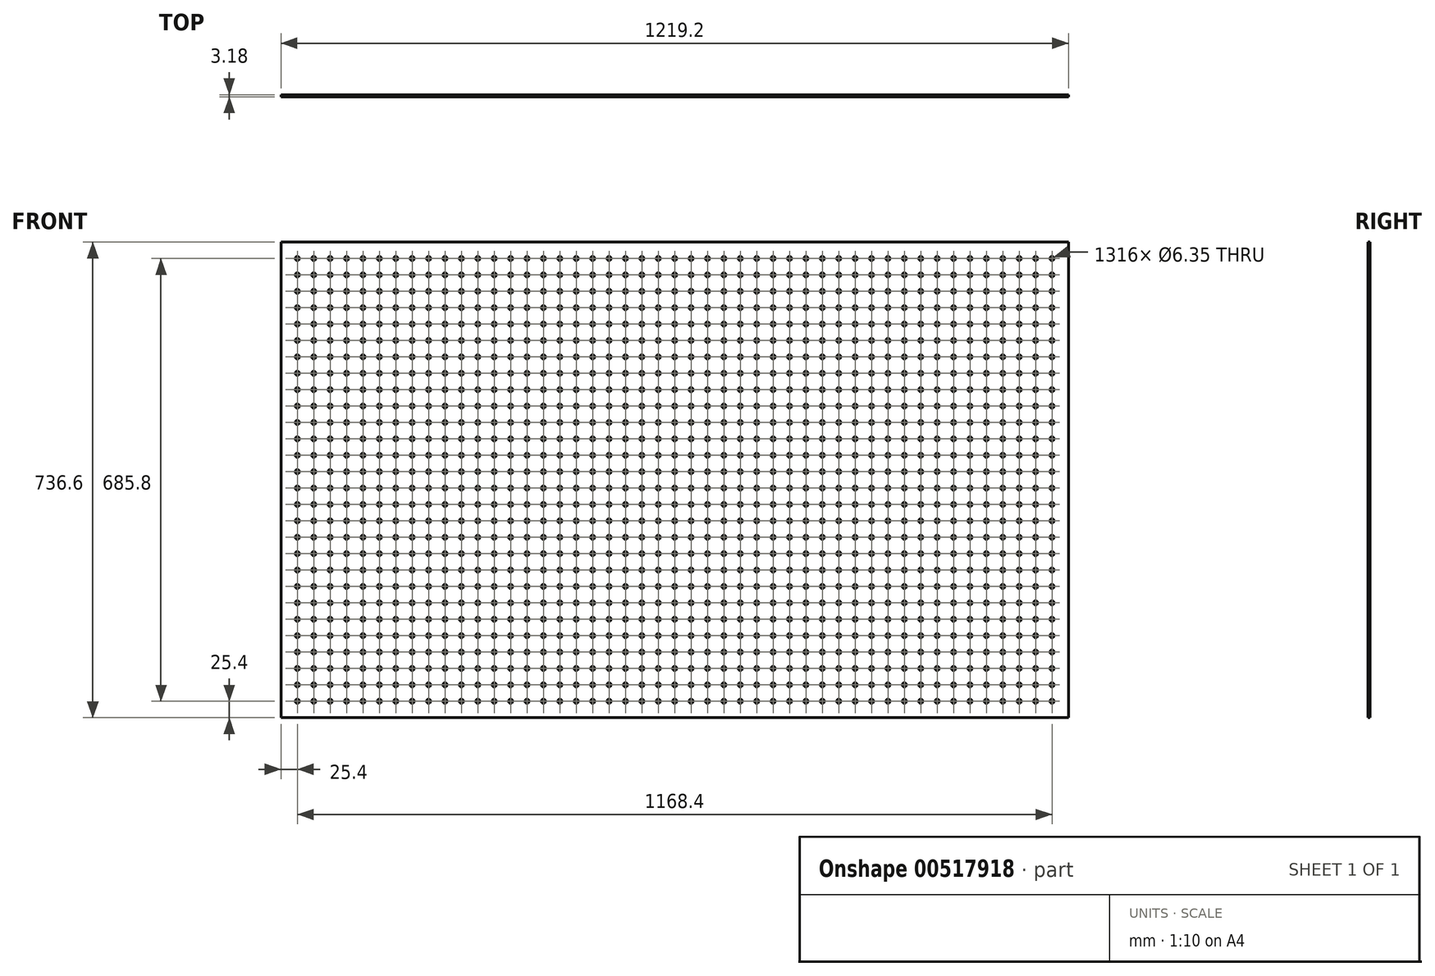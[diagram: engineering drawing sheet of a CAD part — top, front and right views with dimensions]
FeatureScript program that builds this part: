
annotation { "Feature Type Name" : "Feature", "Feature Type Description" : "" }
export const myFeature = defineFeature(function(context is Context, id is Id, definition is map)
    precondition{}
    {
        {
            var Q0;
            Q0=qCreatedBy(makeId("Front.planeOp"),FACE);
            var sketch = newSketch(context, id + "F0", { "sketchPlane" : qUnion([Q0])});
            skLineSegment(sketch, "E0.bottom", {"start": v(609.6, 368.3) * mm, "end": v(-609.6, 368.3) * mm});
            skLineSegment(sketch, "E0.top", {"start": v(609.6, -368.3) * mm, "end": v(-609.6, -368.3) * mm});
            skLineSegment(sketch, "E0.left", {"start": v(609.6, 368.3) * mm, "end": v(609.6, -368.3) * mm});
            skLineSegment(sketch, "E0.right", {"start": v(-609.6, 368.3) * mm, "end": v(-609.6, -368.3) * mm});
            skPoint(sketch, "E0.middle", {"position": v(0, 0) * mm});
            skCircle(sketch, "E1", {"center": v(-584.2, 342.9) * mm, "radius": 3.18 * mm});
            skCircle(sketch, "E2.0.1.0", {"center": v(-584.2, 317.5) * mm, "radius": 3.18 * mm});
            skCircle(sketch, "E2.0.2.0", {"center": v(-584.2, 292.1) * mm, "radius": 3.18 * mm});
            skCircle(sketch, "E2.0.3.0", {"center": v(-584.2, 266.7) * mm, "radius": 3.18 * mm});
            skCircle(sketch, "E2.0.4.0", {"center": v(-584.2, 241.3) * mm, "radius": 3.18 * mm});
            skCircle(sketch, "E2.0.5.0", {"center": v(-584.2, 215.9) * mm, "radius": 3.18 * mm});
            skCircle(sketch, "E2.0.6.0", {"center": v(-584.2, 190.5) * mm, "radius": 3.18 * mm});
            skCircle(sketch, "E2.0.7.0", {"center": v(-584.2, 165.1) * mm, "radius": 3.18 * mm});
            skCircle(sketch, "E2.0.8.0", {"center": v(-584.2, 139.7) * mm, "radius": 3.18 * mm});
            skCircle(sketch, "E2.0.9.0", {"center": v(-584.2, 114.3) * mm, "radius": 3.18 * mm});
            skCircle(sketch, "E2.0.10.0", {"center": v(-584.2, 88.9) * mm, "radius": 3.18 * mm});
            skCircle(sketch, "E2.0.11.0", {"center": v(-584.2, 63.5) * mm, "radius": 3.18 * mm});
            skCircle(sketch, "E2.0.12.0", {"center": v(-584.2, 38.1) * mm, "radius": 3.18 * mm});
            skCircle(sketch, "E2.0.13.0", {"center": v(-584.2, 12.7) * mm, "radius": 3.18 * mm});
            skCircle(sketch, "E2.0.14.0", {"center": v(-584.2, -12.7) * mm, "radius": 3.18 * mm});
            skCircle(sketch, "E2.0.15.0", {"center": v(-584.2, -38.1) * mm, "radius": 3.18 * mm});
            skCircle(sketch, "E2.0.16.0", {"center": v(-584.2, -63.5) * mm, "radius": 3.18 * mm});
            skCircle(sketch, "E2.0.17.0", {"center": v(-584.2, -88.9) * mm, "radius": 3.18 * mm});
            skCircle(sketch, "E2.0.18.0", {"center": v(-584.2, -114.3) * mm, "radius": 3.18 * mm});
            skCircle(sketch, "E2.0.19.0", {"center": v(-584.2, -139.7) * mm, "radius": 3.18 * mm});
            skCircle(sketch, "E2.0.20.0", {"center": v(-584.2, -165.1) * mm, "radius": 3.18 * mm});
            skCircle(sketch, "E2.0.21.0", {"center": v(-584.2, -190.5) * mm, "radius": 3.18 * mm});
            skCircle(sketch, "E2.0.22.0", {"center": v(-584.2, -215.9) * mm, "radius": 3.18 * mm});
            skCircle(sketch, "E2.0.23.0", {"center": v(-584.2, -241.3) * mm, "radius": 3.18 * mm});
            skCircle(sketch, "E2.0.24.0", {"center": v(-584.2, -266.7) * mm, "radius": 3.18 * mm});
            skCircle(sketch, "E2.0.25.0", {"center": v(-584.2, -292.1) * mm, "radius": 3.18 * mm});
            skCircle(sketch, "E2.0.26.0", {"center": v(-584.2, -317.5) * mm, "radius": 3.18 * mm});
            skCircle(sketch, "E2.0.27.0", {"center": v(-584.2, -342.9) * mm, "radius": 3.18 * mm});
            skCircle(sketch, "E2.1.0.0", {"center": v(-558.8, 342.9) * mm, "radius": 3.18 * mm});
            skCircle(sketch, "E2.1.1.0", {"center": v(-558.8, 317.5) * mm, "radius": 3.18 * mm});
            skCircle(sketch, "E2.1.2.0", {"center": v(-558.8, 292.1) * mm, "radius": 3.18 * mm});
            skCircle(sketch, "E2.1.3.0", {"center": v(-558.8, 266.7) * mm, "radius": 3.18 * mm});
            skCircle(sketch, "E2.1.4.0", {"center": v(-558.8, 241.3) * mm, "radius": 3.18 * mm});
            skCircle(sketch, "E2.1.5.0", {"center": v(-558.8, 215.9) * mm, "radius": 3.18 * mm});
            skCircle(sketch, "E2.1.6.0", {"center": v(-558.8, 190.5) * mm, "radius": 3.18 * mm});
            skCircle(sketch, "E2.1.7.0", {"center": v(-558.8, 165.1) * mm, "radius": 3.18 * mm});
            skCircle(sketch, "E2.1.8.0", {"center": v(-558.8, 139.7) * mm, "radius": 3.18 * mm});
            skCircle(sketch, "E2.1.9.0", {"center": v(-558.8, 114.3) * mm, "radius": 3.18 * mm});
            skCircle(sketch, "E2.1.10.0", {"center": v(-558.8, 88.9) * mm, "radius": 3.18 * mm});
            skCircle(sketch, "E2.1.11.0", {"center": v(-558.8, 63.5) * mm, "radius": 3.18 * mm});
            skCircle(sketch, "E2.1.12.0", {"center": v(-558.8, 38.1) * mm, "radius": 3.18 * mm});
            skCircle(sketch, "E2.1.13.0", {"center": v(-558.8, 12.7) * mm, "radius": 3.18 * mm});
            skCircle(sketch, "E2.1.14.0", {"center": v(-558.8, -12.7) * mm, "radius": 3.18 * mm});
            skCircle(sketch, "E2.1.15.0", {"center": v(-558.8, -38.1) * mm, "radius": 3.18 * mm});
            skCircle(sketch, "E2.1.16.0", {"center": v(-558.8, -63.5) * mm, "radius": 3.18 * mm});
            skCircle(sketch, "E2.1.17.0", {"center": v(-558.8, -88.9) * mm, "radius": 3.18 * mm});
            skCircle(sketch, "E2.1.18.0", {"center": v(-558.8, -114.3) * mm, "radius": 3.18 * mm});
            skCircle(sketch, "E2.1.19.0", {"center": v(-558.8, -139.7) * mm, "radius": 3.18 * mm});
            skCircle(sketch, "E2.1.20.0", {"center": v(-558.8, -165.1) * mm, "radius": 3.18 * mm});
            skCircle(sketch, "E2.1.21.0", {"center": v(-558.8, -190.5) * mm, "radius": 3.18 * mm});
            skCircle(sketch, "E2.1.22.0", {"center": v(-558.8, -215.9) * mm, "radius": 3.18 * mm});
            skCircle(sketch, "E2.1.23.0", {"center": v(-558.8, -241.3) * mm, "radius": 3.18 * mm});
            skCircle(sketch, "E2.1.24.0", {"center": v(-558.8, -266.7) * mm, "radius": 3.18 * mm});
            skCircle(sketch, "E2.1.25.0", {"center": v(-558.8, -292.1) * mm, "radius": 3.18 * mm});
            skCircle(sketch, "E2.1.26.0", {"center": v(-558.8, -317.5) * mm, "radius": 3.18 * mm});
            skCircle(sketch, "E2.1.27.0", {"center": v(-558.8, -342.9) * mm, "radius": 3.18 * mm});
            skCircle(sketch, "E2.2.0.0", {"center": v(-533.4, 342.9) * mm, "radius": 3.18 * mm});
            skCircle(sketch, "E2.2.1.0", {"center": v(-533.4, 317.5) * mm, "radius": 3.18 * mm});
            skCircle(sketch, "E2.2.2.0", {"center": v(-533.4, 292.1) * mm, "radius": 3.18 * mm});
            skCircle(sketch, "E2.2.3.0", {"center": v(-533.4, 266.7) * mm, "radius": 3.18 * mm});
            skCircle(sketch, "E2.2.4.0", {"center": v(-533.4, 241.3) * mm, "radius": 3.18 * mm});
            skCircle(sketch, "E2.2.5.0", {"center": v(-533.4, 215.9) * mm, "radius": 3.18 * mm});
            skCircle(sketch, "E2.2.6.0", {"center": v(-533.4, 190.5) * mm, "radius": 3.18 * mm});
            skCircle(sketch, "E2.2.7.0", {"center": v(-533.4, 165.1) * mm, "radius": 3.18 * mm});
            skCircle(sketch, "E2.2.8.0", {"center": v(-533.4, 139.7) * mm, "radius": 3.18 * mm});
            skCircle(sketch, "E2.2.9.0", {"center": v(-533.4, 114.3) * mm, "radius": 3.18 * mm});
            skCircle(sketch, "E2.2.10.0", {"center": v(-533.4, 88.9) * mm, "radius": 3.18 * mm});
            skCircle(sketch, "E2.2.11.0", {"center": v(-533.4, 63.5) * mm, "radius": 3.18 * mm});
            skCircle(sketch, "E2.2.12.0", {"center": v(-533.4, 38.1) * mm, "radius": 3.18 * mm});
            skCircle(sketch, "E2.2.13.0", {"center": v(-533.4, 12.7) * mm, "radius": 3.18 * mm});
            skCircle(sketch, "E2.2.14.0", {"center": v(-533.4, -12.7) * mm, "radius": 3.18 * mm});
            skCircle(sketch, "E2.2.15.0", {"center": v(-533.4, -38.1) * mm, "radius": 3.18 * mm});
            skCircle(sketch, "E2.2.16.0", {"center": v(-533.4, -63.5) * mm, "radius": 3.18 * mm});
            skCircle(sketch, "E2.2.17.0", {"center": v(-533.4, -88.9) * mm, "radius": 3.18 * mm});
            skCircle(sketch, "E2.2.18.0", {"center": v(-533.4, -114.3) * mm, "radius": 3.18 * mm});
            skCircle(sketch, "E2.2.19.0", {"center": v(-533.4, -139.7) * mm, "radius": 3.18 * mm});
            skCircle(sketch, "E2.2.20.0", {"center": v(-533.4, -165.1) * mm, "radius": 3.18 * mm});
            skCircle(sketch, "E2.2.21.0", {"center": v(-533.4, -190.5) * mm, "radius": 3.18 * mm});
            skCircle(sketch, "E2.2.22.0", {"center": v(-533.4, -215.9) * mm, "radius": 3.18 * mm});
            skCircle(sketch, "E2.2.23.0", {"center": v(-533.4, -241.3) * mm, "radius": 3.18 * mm});
            skCircle(sketch, "E2.2.24.0", {"center": v(-533.4, -266.7) * mm, "radius": 3.18 * mm});
            skCircle(sketch, "E2.2.25.0", {"center": v(-533.4, -292.1) * mm, "radius": 3.18 * mm});
            skCircle(sketch, "E2.2.26.0", {"center": v(-533.4, -317.5) * mm, "radius": 3.18 * mm});
            skCircle(sketch, "E2.2.27.0", {"center": v(-533.4, -342.9) * mm, "radius": 3.18 * mm});
            skCircle(sketch, "E2.3.0.0", {"center": v(-508, 342.9) * mm, "radius": 3.18 * mm});
            skCircle(sketch, "E2.3.1.0", {"center": v(-508, 317.5) * mm, "radius": 3.18 * mm});
            skCircle(sketch, "E2.3.2.0", {"center": v(-508, 292.1) * mm, "radius": 3.18 * mm});
            skCircle(sketch, "E2.3.3.0", {"center": v(-508, 266.7) * mm, "radius": 3.18 * mm});
            skCircle(sketch, "E2.3.4.0", {"center": v(-508, 241.3) * mm, "radius": 3.18 * mm});
            skCircle(sketch, "E2.3.5.0", {"center": v(-508, 215.9) * mm, "radius": 3.18 * mm});
            skCircle(sketch, "E2.3.6.0", {"center": v(-508, 190.5) * mm, "radius": 3.18 * mm});
            skCircle(sketch, "E2.3.7.0", {"center": v(-508, 165.1) * mm, "radius": 3.18 * mm});
            skCircle(sketch, "E2.3.8.0", {"center": v(-508, 139.7) * mm, "radius": 3.18 * mm});
            skCircle(sketch, "E2.3.9.0", {"center": v(-508, 114.3) * mm, "radius": 3.18 * mm});
            skCircle(sketch, "E2.3.10.0", {"center": v(-508, 88.9) * mm, "radius": 3.18 * mm});
            skCircle(sketch, "E2.3.11.0", {"center": v(-508, 63.5) * mm, "radius": 3.18 * mm});
            skCircle(sketch, "E2.3.12.0", {"center": v(-508, 38.1) * mm, "radius": 3.18 * mm});
            skCircle(sketch, "E2.3.13.0", {"center": v(-508, 12.7) * mm, "radius": 3.18 * mm});
            skCircle(sketch, "E2.3.14.0", {"center": v(-508, -12.7) * mm, "radius": 3.18 * mm});
            skCircle(sketch, "E2.3.15.0", {"center": v(-508, -38.1) * mm, "radius": 3.18 * mm});
            skCircle(sketch, "E2.3.16.0", {"center": v(-508, -63.5) * mm, "radius": 3.18 * mm});
            skCircle(sketch, "E2.3.17.0", {"center": v(-508, -88.9) * mm, "radius": 3.18 * mm});
            skCircle(sketch, "E2.3.18.0", {"center": v(-508, -114.3) * mm, "radius": 3.18 * mm});
            skCircle(sketch, "E2.3.19.0", {"center": v(-508, -139.7) * mm, "radius": 3.18 * mm});
            skCircle(sketch, "E2.3.20.0", {"center": v(-508, -165.1) * mm, "radius": 3.18 * mm});
            skCircle(sketch, "E2.3.21.0", {"center": v(-508, -190.5) * mm, "radius": 3.18 * mm});
            skCircle(sketch, "E2.3.22.0", {"center": v(-508, -215.9) * mm, "radius": 3.18 * mm});
            skCircle(sketch, "E2.3.23.0", {"center": v(-508, -241.3) * mm, "radius": 3.18 * mm});
            skCircle(sketch, "E2.3.24.0", {"center": v(-508, -266.7) * mm, "radius": 3.18 * mm});
            skCircle(sketch, "E2.3.25.0", {"center": v(-508, -292.1) * mm, "radius": 3.18 * mm});
            skCircle(sketch, "E2.3.26.0", {"center": v(-508, -317.5) * mm, "radius": 3.18 * mm});
            skCircle(sketch, "E2.3.27.0", {"center": v(-508, -342.9) * mm, "radius": 3.18 * mm});
            skCircle(sketch, "E2.4.0.0", {"center": v(-482.6, 342.9) * mm, "radius": 3.18 * mm});
            skCircle(sketch, "E2.4.1.0", {"center": v(-482.6, 317.5) * mm, "radius": 3.18 * mm});
            skCircle(sketch, "E2.4.2.0", {"center": v(-482.6, 292.1) * mm, "radius": 3.18 * mm});
            skCircle(sketch, "E2.4.3.0", {"center": v(-482.6, 266.7) * mm, "radius": 3.18 * mm});
            skCircle(sketch, "E2.4.4.0", {"center": v(-482.6, 241.3) * mm, "radius": 3.18 * mm});
            skCircle(sketch, "E2.4.5.0", {"center": v(-482.6, 215.9) * mm, "radius": 3.18 * mm});
            skCircle(sketch, "E2.4.6.0", {"center": v(-482.6, 190.5) * mm, "radius": 3.18 * mm});
            skCircle(sketch, "E2.4.7.0", {"center": v(-482.6, 165.1) * mm, "radius": 3.18 * mm});
            skCircle(sketch, "E2.4.8.0", {"center": v(-482.6, 139.7) * mm, "radius": 3.18 * mm});
            skCircle(sketch, "E2.4.9.0", {"center": v(-482.6, 114.3) * mm, "radius": 3.18 * mm});
            skCircle(sketch, "E2.4.10.0", {"center": v(-482.6, 88.9) * mm, "radius": 3.18 * mm});
            skCircle(sketch, "E2.4.11.0", {"center": v(-482.6, 63.5) * mm, "radius": 3.18 * mm});
            skCircle(sketch, "E2.4.12.0", {"center": v(-482.6, 38.1) * mm, "radius": 3.18 * mm});
            skCircle(sketch, "E2.4.13.0", {"center": v(-482.6, 12.7) * mm, "radius": 3.18 * mm});
            skCircle(sketch, "E2.4.14.0", {"center": v(-482.6, -12.7) * mm, "radius": 3.18 * mm});
            skCircle(sketch, "E2.4.15.0", {"center": v(-482.6, -38.1) * mm, "radius": 3.18 * mm});
            skCircle(sketch, "E2.4.16.0", {"center": v(-482.6, -63.5) * mm, "radius": 3.18 * mm});
            skCircle(sketch, "E2.4.17.0", {"center": v(-482.6, -88.9) * mm, "radius": 3.18 * mm});
            skCircle(sketch, "E2.4.18.0", {"center": v(-482.6, -114.3) * mm, "radius": 3.18 * mm});
            skCircle(sketch, "E2.4.19.0", {"center": v(-482.6, -139.7) * mm, "radius": 3.18 * mm});
            skCircle(sketch, "E2.4.20.0", {"center": v(-482.6, -165.1) * mm, "radius": 3.18 * mm});
            skCircle(sketch, "E2.4.21.0", {"center": v(-482.6, -190.5) * mm, "radius": 3.18 * mm});
            skCircle(sketch, "E2.4.22.0", {"center": v(-482.6, -215.9) * mm, "radius": 3.18 * mm});
            skCircle(sketch, "E2.4.23.0", {"center": v(-482.6, -241.3) * mm, "radius": 3.18 * mm});
            skCircle(sketch, "E2.4.24.0", {"center": v(-482.6, -266.7) * mm, "radius": 3.18 * mm});
            skCircle(sketch, "E2.4.25.0", {"center": v(-482.6, -292.1) * mm, "radius": 3.18 * mm});
            skCircle(sketch, "E2.4.26.0", {"center": v(-482.6, -317.5) * mm, "radius": 3.18 * mm});
            skCircle(sketch, "E2.4.27.0", {"center": v(-482.6, -342.9) * mm, "radius": 3.18 * mm});
            skCircle(sketch, "E2.5.0.0", {"center": v(-457.2, 342.9) * mm, "radius": 3.18 * mm});
            skCircle(sketch, "E2.5.1.0", {"center": v(-457.2, 317.5) * mm, "radius": 3.18 * mm});
            skCircle(sketch, "E2.5.2.0", {"center": v(-457.2, 292.1) * mm, "radius": 3.18 * mm});
            skCircle(sketch, "E2.5.3.0", {"center": v(-457.2, 266.7) * mm, "radius": 3.18 * mm});
            skCircle(sketch, "E2.5.4.0", {"center": v(-457.2, 241.3) * mm, "radius": 3.18 * mm});
            skCircle(sketch, "E2.5.5.0", {"center": v(-457.2, 215.9) * mm, "radius": 3.18 * mm});
            skCircle(sketch, "E2.5.6.0", {"center": v(-457.2, 190.5) * mm, "radius": 3.18 * mm});
            skCircle(sketch, "E2.5.7.0", {"center": v(-457.2, 165.1) * mm, "radius": 3.18 * mm});
            skCircle(sketch, "E2.5.8.0", {"center": v(-457.2, 139.7) * mm, "radius": 3.18 * mm});
            skCircle(sketch, "E2.5.9.0", {"center": v(-457.2, 114.3) * mm, "radius": 3.18 * mm});
            skCircle(sketch, "E2.5.10.0", {"center": v(-457.2, 88.9) * mm, "radius": 3.18 * mm});
            skCircle(sketch, "E2.5.11.0", {"center": v(-457.2, 63.5) * mm, "radius": 3.18 * mm});
            skCircle(sketch, "E2.5.12.0", {"center": v(-457.2, 38.1) * mm, "radius": 3.18 * mm});
            skCircle(sketch, "E2.5.13.0", {"center": v(-457.2, 12.7) * mm, "radius": 3.18 * mm});
            skCircle(sketch, "E2.5.14.0", {"center": v(-457.2, -12.7) * mm, "radius": 3.18 * mm});
            skCircle(sketch, "E2.5.15.0", {"center": v(-457.2, -38.1) * mm, "radius": 3.18 * mm});
            skCircle(sketch, "E2.5.16.0", {"center": v(-457.2, -63.5) * mm, "radius": 3.18 * mm});
            skCircle(sketch, "E2.5.17.0", {"center": v(-457.2, -88.9) * mm, "radius": 3.18 * mm});
            skCircle(sketch, "E2.5.18.0", {"center": v(-457.2, -114.3) * mm, "radius": 3.18 * mm});
            skCircle(sketch, "E2.5.19.0", {"center": v(-457.2, -139.7) * mm, "radius": 3.18 * mm});
            skCircle(sketch, "E2.5.20.0", {"center": v(-457.2, -165.1) * mm, "radius": 3.18 * mm});
            skCircle(sketch, "E2.5.21.0", {"center": v(-457.2, -190.5) * mm, "radius": 3.18 * mm});
            skCircle(sketch, "E2.5.22.0", {"center": v(-457.2, -215.9) * mm, "radius": 3.18 * mm});
            skCircle(sketch, "E2.5.23.0", {"center": v(-457.2, -241.3) * mm, "radius": 3.18 * mm});
            skCircle(sketch, "E2.5.24.0", {"center": v(-457.2, -266.7) * mm, "radius": 3.18 * mm});
            skCircle(sketch, "E2.5.25.0", {"center": v(-457.2, -292.1) * mm, "radius": 3.18 * mm});
            skCircle(sketch, "E2.5.26.0", {"center": v(-457.2, -317.5) * mm, "radius": 3.18 * mm});
            skCircle(sketch, "E2.5.27.0", {"center": v(-457.2, -342.9) * mm, "radius": 3.18 * mm});
            skCircle(sketch, "E2.6.0.0", {"center": v(-431.8, 342.9) * mm, "radius": 3.18 * mm});
            skCircle(sketch, "E2.6.1.0", {"center": v(-431.8, 317.5) * mm, "radius": 3.18 * mm});
            skCircle(sketch, "E2.6.2.0", {"center": v(-431.8, 292.1) * mm, "radius": 3.18 * mm});
            skCircle(sketch, "E2.6.3.0", {"center": v(-431.8, 266.7) * mm, "radius": 3.18 * mm});
            skCircle(sketch, "E2.6.4.0", {"center": v(-431.8, 241.3) * mm, "radius": 3.18 * mm});
            skCircle(sketch, "E2.6.5.0", {"center": v(-431.8, 215.9) * mm, "radius": 3.18 * mm});
            skCircle(sketch, "E2.6.6.0", {"center": v(-431.8, 190.5) * mm, "radius": 3.18 * mm});
            skCircle(sketch, "E2.6.7.0", {"center": v(-431.8, 165.1) * mm, "radius": 3.18 * mm});
            skCircle(sketch, "E2.6.8.0", {"center": v(-431.8, 139.7) * mm, "radius": 3.18 * mm});
            skCircle(sketch, "E2.6.9.0", {"center": v(-431.8, 114.3) * mm, "radius": 3.18 * mm});
            skCircle(sketch, "E2.6.10.0", {"center": v(-431.8, 88.9) * mm, "radius": 3.18 * mm});
            skCircle(sketch, "E2.6.11.0", {"center": v(-431.8, 63.5) * mm, "radius": 3.18 * mm});
            skCircle(sketch, "E2.6.12.0", {"center": v(-431.8, 38.1) * mm, "radius": 3.18 * mm});
            skCircle(sketch, "E2.6.13.0", {"center": v(-431.8, 12.7) * mm, "radius": 3.18 * mm});
            skCircle(sketch, "E2.6.14.0", {"center": v(-431.8, -12.7) * mm, "radius": 3.18 * mm});
            skCircle(sketch, "E2.6.15.0", {"center": v(-431.8, -38.1) * mm, "radius": 3.18 * mm});
            skCircle(sketch, "E2.6.16.0", {"center": v(-431.8, -63.5) * mm, "radius": 3.18 * mm});
            skCircle(sketch, "E2.6.17.0", {"center": v(-431.8, -88.9) * mm, "radius": 3.18 * mm});
            skCircle(sketch, "E2.6.18.0", {"center": v(-431.8, -114.3) * mm, "radius": 3.18 * mm});
            skCircle(sketch, "E2.6.19.0", {"center": v(-431.8, -139.7) * mm, "radius": 3.18 * mm});
            skCircle(sketch, "E2.6.20.0", {"center": v(-431.8, -165.1) * mm, "radius": 3.18 * mm});
            skCircle(sketch, "E2.6.21.0", {"center": v(-431.8, -190.5) * mm, "radius": 3.18 * mm});
            skCircle(sketch, "E2.6.22.0", {"center": v(-431.8, -215.9) * mm, "radius": 3.18 * mm});
            skCircle(sketch, "E2.6.23.0", {"center": v(-431.8, -241.3) * mm, "radius": 3.18 * mm});
            skCircle(sketch, "E2.6.24.0", {"center": v(-431.8, -266.7) * mm, "radius": 3.18 * mm});
            skCircle(sketch, "E2.6.25.0", {"center": v(-431.8, -292.1) * mm, "radius": 3.18 * mm});
            skCircle(sketch, "E2.6.26.0", {"center": v(-431.8, -317.5) * mm, "radius": 3.18 * mm});
            skCircle(sketch, "E2.6.27.0", {"center": v(-431.8, -342.9) * mm, "radius": 3.18 * mm});
            skCircle(sketch, "E2.7.0.0", {"center": v(-406.4, 342.9) * mm, "radius": 3.18 * mm});
            skCircle(sketch, "E2.7.1.0", {"center": v(-406.4, 317.5) * mm, "radius": 3.18 * mm});
            skCircle(sketch, "E2.7.2.0", {"center": v(-406.4, 292.1) * mm, "radius": 3.18 * mm});
            skCircle(sketch, "E2.7.3.0", {"center": v(-406.4, 266.7) * mm, "radius": 3.18 * mm});
            skCircle(sketch, "E2.7.4.0", {"center": v(-406.4, 241.3) * mm, "radius": 3.18 * mm});
            skCircle(sketch, "E2.7.5.0", {"center": v(-406.4, 215.9) * mm, "radius": 3.18 * mm});
            skCircle(sketch, "E2.7.6.0", {"center": v(-406.4, 190.5) * mm, "radius": 3.18 * mm});
            skCircle(sketch, "E2.7.7.0", {"center": v(-406.4, 165.1) * mm, "radius": 3.18 * mm});
            skCircle(sketch, "E2.7.8.0", {"center": v(-406.4, 139.7) * mm, "radius": 3.18 * mm});
            skCircle(sketch, "E2.7.9.0", {"center": v(-406.4, 114.3) * mm, "radius": 3.18 * mm});
            skCircle(sketch, "E2.7.10.0", {"center": v(-406.4, 88.9) * mm, "radius": 3.18 * mm});
            skCircle(sketch, "E2.7.11.0", {"center": v(-406.4, 63.5) * mm, "radius": 3.18 * mm});
            skCircle(sketch, "E2.7.12.0", {"center": v(-406.4, 38.1) * mm, "radius": 3.18 * mm});
            skCircle(sketch, "E2.7.13.0", {"center": v(-406.4, 12.7) * mm, "radius": 3.18 * mm});
            skCircle(sketch, "E2.7.14.0", {"center": v(-406.4, -12.7) * mm, "radius": 3.18 * mm});
            skCircle(sketch, "E2.7.15.0", {"center": v(-406.4, -38.1) * mm, "radius": 3.18 * mm});
            skCircle(sketch, "E2.7.16.0", {"center": v(-406.4, -63.5) * mm, "radius": 3.18 * mm});
            skCircle(sketch, "E2.7.17.0", {"center": v(-406.4, -88.9) * mm, "radius": 3.18 * mm});
            skCircle(sketch, "E2.7.18.0", {"center": v(-406.4, -114.3) * mm, "radius": 3.18 * mm});
            skCircle(sketch, "E2.7.19.0", {"center": v(-406.4, -139.7) * mm, "radius": 3.18 * mm});
            skCircle(sketch, "E2.7.20.0", {"center": v(-406.4, -165.1) * mm, "radius": 3.18 * mm});
            skCircle(sketch, "E2.7.21.0", {"center": v(-406.4, -190.5) * mm, "radius": 3.18 * mm});
            skCircle(sketch, "E2.7.22.0", {"center": v(-406.4, -215.9) * mm, "radius": 3.18 * mm});
            skCircle(sketch, "E2.7.23.0", {"center": v(-406.4, -241.3) * mm, "radius": 3.18 * mm});
            skCircle(sketch, "E2.7.24.0", {"center": v(-406.4, -266.7) * mm, "radius": 3.18 * mm});
            skCircle(sketch, "E2.7.25.0", {"center": v(-406.4, -292.1) * mm, "radius": 3.18 * mm});
            skCircle(sketch, "E2.7.26.0", {"center": v(-406.4, -317.5) * mm, "radius": 3.18 * mm});
            skCircle(sketch, "E2.7.27.0", {"center": v(-406.4, -342.9) * mm, "radius": 3.18 * mm});
            skCircle(sketch, "E2.8.0.0", {"center": v(-381, 342.9) * mm, "radius": 3.18 * mm});
            skCircle(sketch, "E2.8.1.0", {"center": v(-381, 317.5) * mm, "radius": 3.18 * mm});
            skCircle(sketch, "E2.8.2.0", {"center": v(-381, 292.1) * mm, "radius": 3.18 * mm});
            skCircle(sketch, "E2.8.3.0", {"center": v(-381, 266.7) * mm, "radius": 3.18 * mm});
            skCircle(sketch, "E2.8.4.0", {"center": v(-381, 241.3) * mm, "radius": 3.18 * mm});
            skCircle(sketch, "E2.8.5.0", {"center": v(-381, 215.9) * mm, "radius": 3.18 * mm});
            skCircle(sketch, "E2.8.6.0", {"center": v(-381, 190.5) * mm, "radius": 3.18 * mm});
            skCircle(sketch, "E2.8.7.0", {"center": v(-381, 165.1) * mm, "radius": 3.18 * mm});
            skCircle(sketch, "E2.8.8.0", {"center": v(-381, 139.7) * mm, "radius": 3.18 * mm});
            skCircle(sketch, "E2.8.9.0", {"center": v(-381, 114.3) * mm, "radius": 3.18 * mm});
            skCircle(sketch, "E2.8.10.0", {"center": v(-381, 88.9) * mm, "radius": 3.18 * mm});
            skCircle(sketch, "E2.8.11.0", {"center": v(-381, 63.5) * mm, "radius": 3.18 * mm});
            skCircle(sketch, "E2.8.12.0", {"center": v(-381, 38.1) * mm, "radius": 3.18 * mm});
            skCircle(sketch, "E2.8.13.0", {"center": v(-381, 12.7) * mm, "radius": 3.18 * mm});
            skCircle(sketch, "E2.8.14.0", {"center": v(-381, -12.7) * mm, "radius": 3.18 * mm});
            skCircle(sketch, "E2.8.15.0", {"center": v(-381, -38.1) * mm, "radius": 3.18 * mm});
            skCircle(sketch, "E2.8.16.0", {"center": v(-381, -63.5) * mm, "radius": 3.18 * mm});
            skCircle(sketch, "E2.8.17.0", {"center": v(-381, -88.9) * mm, "radius": 3.18 * mm});
            skCircle(sketch, "E2.8.18.0", {"center": v(-381, -114.3) * mm, "radius": 3.18 * mm});
            skCircle(sketch, "E2.8.19.0", {"center": v(-381, -139.7) * mm, "radius": 3.18 * mm});
            skCircle(sketch, "E2.8.20.0", {"center": v(-381, -165.1) * mm, "radius": 3.18 * mm});
            skCircle(sketch, "E2.8.21.0", {"center": v(-381, -190.5) * mm, "radius": 3.18 * mm});
            skCircle(sketch, "E2.8.22.0", {"center": v(-381, -215.9) * mm, "radius": 3.18 * mm});
            skCircle(sketch, "E2.8.23.0", {"center": v(-381, -241.3) * mm, "radius": 3.18 * mm});
            skCircle(sketch, "E2.8.24.0", {"center": v(-381, -266.7) * mm, "radius": 3.18 * mm});
            skCircle(sketch, "E2.8.25.0", {"center": v(-381, -292.1) * mm, "radius": 3.18 * mm});
            skCircle(sketch, "E2.8.26.0", {"center": v(-381, -317.5) * mm, "radius": 3.18 * mm});
            skCircle(sketch, "E2.8.27.0", {"center": v(-381, -342.9) * mm, "radius": 3.18 * mm});
            skCircle(sketch, "E2.9.0.0", {"center": v(-355.6, 342.9) * mm, "radius": 3.18 * mm});
            skCircle(sketch, "E2.9.1.0", {"center": v(-355.6, 317.5) * mm, "radius": 3.18 * mm});
            skCircle(sketch, "E2.9.2.0", {"center": v(-355.6, 292.1) * mm, "radius": 3.18 * mm});
            skCircle(sketch, "E2.9.3.0", {"center": v(-355.6, 266.7) * mm, "radius": 3.18 * mm});
            skCircle(sketch, "E2.9.4.0", {"center": v(-355.6, 241.3) * mm, "radius": 3.18 * mm});
            skCircle(sketch, "E2.9.5.0", {"center": v(-355.6, 215.9) * mm, "radius": 3.18 * mm});
            skCircle(sketch, "E2.9.6.0", {"center": v(-355.6, 190.5) * mm, "radius": 3.18 * mm});
            skCircle(sketch, "E2.9.7.0", {"center": v(-355.6, 165.1) * mm, "radius": 3.18 * mm});
            skCircle(sketch, "E2.9.8.0", {"center": v(-355.6, 139.7) * mm, "radius": 3.18 * mm});
            skCircle(sketch, "E2.9.9.0", {"center": v(-355.6, 114.3) * mm, "radius": 3.18 * mm});
            skCircle(sketch, "E2.9.10.0", {"center": v(-355.6, 88.9) * mm, "radius": 3.18 * mm});
            skCircle(sketch, "E2.9.11.0", {"center": v(-355.6, 63.5) * mm, "radius": 3.18 * mm});
            skCircle(sketch, "E2.9.12.0", {"center": v(-355.6, 38.1) * mm, "radius": 3.18 * mm});
            skCircle(sketch, "E2.9.13.0", {"center": v(-355.6, 12.7) * mm, "radius": 3.18 * mm});
            skCircle(sketch, "E2.9.14.0", {"center": v(-355.6, -12.7) * mm, "radius": 3.18 * mm});
            skCircle(sketch, "E2.9.15.0", {"center": v(-355.6, -38.1) * mm, "radius": 3.18 * mm});
            skCircle(sketch, "E2.9.16.0", {"center": v(-355.6, -63.5) * mm, "radius": 3.18 * mm});
            skCircle(sketch, "E2.9.17.0", {"center": v(-355.6, -88.9) * mm, "radius": 3.18 * mm});
            skCircle(sketch, "E2.9.18.0", {"center": v(-355.6, -114.3) * mm, "radius": 3.18 * mm});
            skCircle(sketch, "E2.9.19.0", {"center": v(-355.6, -139.7) * mm, "radius": 3.18 * mm});
            skCircle(sketch, "E2.9.20.0", {"center": v(-355.6, -165.1) * mm, "radius": 3.18 * mm});
            skCircle(sketch, "E2.9.21.0", {"center": v(-355.6, -190.5) * mm, "radius": 3.18 * mm});
            skCircle(sketch, "E2.9.22.0", {"center": v(-355.6, -215.9) * mm, "radius": 3.18 * mm});
            skCircle(sketch, "E2.9.23.0", {"center": v(-355.6, -241.3) * mm, "radius": 3.18 * mm});
            skCircle(sketch, "E2.9.24.0", {"center": v(-355.6, -266.7) * mm, "radius": 3.18 * mm});
            skCircle(sketch, "E2.9.25.0", {"center": v(-355.6, -292.1) * mm, "radius": 3.18 * mm});
            skCircle(sketch, "E2.9.26.0", {"center": v(-355.6, -317.5) * mm, "radius": 3.18 * mm});
            skCircle(sketch, "E2.9.27.0", {"center": v(-355.6, -342.9) * mm, "radius": 3.18 * mm});
            skCircle(sketch, "E2.10.0.0", {"center": v(-330.2, 342.9) * mm, "radius": 3.18 * mm});
            skCircle(sketch, "E2.10.1.0", {"center": v(-330.2, 317.5) * mm, "radius": 3.18 * mm});
            skCircle(sketch, "E2.10.2.0", {"center": v(-330.2, 292.1) * mm, "radius": 3.18 * mm});
            skCircle(sketch, "E2.10.3.0", {"center": v(-330.2, 266.7) * mm, "radius": 3.18 * mm});
            skCircle(sketch, "E2.10.4.0", {"center": v(-330.2, 241.3) * mm, "radius": 3.18 * mm});
            skCircle(sketch, "E2.10.5.0", {"center": v(-330.2, 215.9) * mm, "radius": 3.18 * mm});
            skCircle(sketch, "E2.10.6.0", {"center": v(-330.2, 190.5) * mm, "radius": 3.18 * mm});
            skCircle(sketch, "E2.10.7.0", {"center": v(-330.2, 165.1) * mm, "radius": 3.18 * mm});
            skCircle(sketch, "E2.10.8.0", {"center": v(-330.2, 139.7) * mm, "radius": 3.18 * mm});
            skCircle(sketch, "E2.10.9.0", {"center": v(-330.2, 114.3) * mm, "radius": 3.18 * mm});
            skCircle(sketch, "E2.10.10.0", {"center": v(-330.2, 88.9) * mm, "radius": 3.18 * mm});
            skCircle(sketch, "E2.10.11.0", {"center": v(-330.2, 63.5) * mm, "radius": 3.18 * mm});
            skCircle(sketch, "E2.10.12.0", {"center": v(-330.2, 38.1) * mm, "radius": 3.18 * mm});
            skCircle(sketch, "E2.10.13.0", {"center": v(-330.2, 12.7) * mm, "radius": 3.18 * mm});
            skCircle(sketch, "E2.10.14.0", {"center": v(-330.2, -12.7) * mm, "radius": 3.18 * mm});
            skCircle(sketch, "E2.10.15.0", {"center": v(-330.2, -38.1) * mm, "radius": 3.18 * mm});
            skCircle(sketch, "E2.10.16.0", {"center": v(-330.2, -63.5) * mm, "radius": 3.18 * mm});
            skCircle(sketch, "E2.10.17.0", {"center": v(-330.2, -88.9) * mm, "radius": 3.18 * mm});
            skCircle(sketch, "E2.10.18.0", {"center": v(-330.2, -114.3) * mm, "radius": 3.18 * mm});
            skCircle(sketch, "E2.10.19.0", {"center": v(-330.2, -139.7) * mm, "radius": 3.18 * mm});
            skCircle(sketch, "E2.10.20.0", {"center": v(-330.2, -165.1) * mm, "radius": 3.18 * mm});
            skCircle(sketch, "E2.10.21.0", {"center": v(-330.2, -190.5) * mm, "radius": 3.18 * mm});
            skCircle(sketch, "E2.10.22.0", {"center": v(-330.2, -215.9) * mm, "radius": 3.18 * mm});
            skCircle(sketch, "E2.10.23.0", {"center": v(-330.2, -241.3) * mm, "radius": 3.18 * mm});
            skCircle(sketch, "E2.10.24.0", {"center": v(-330.2, -266.7) * mm, "radius": 3.18 * mm});
            skCircle(sketch, "E2.10.25.0", {"center": v(-330.2, -292.1) * mm, "radius": 3.18 * mm});
            skCircle(sketch, "E2.10.26.0", {"center": v(-330.2, -317.5) * mm, "radius": 3.18 * mm});
            skCircle(sketch, "E2.10.27.0", {"center": v(-330.2, -342.9) * mm, "radius": 3.18 * mm});
            skCircle(sketch, "E2.11.0.0", {"center": v(-304.8, 342.9) * mm, "radius": 3.18 * mm});
            skCircle(sketch, "E2.11.1.0", {"center": v(-304.8, 317.5) * mm, "radius": 3.18 * mm});
            skCircle(sketch, "E2.11.2.0", {"center": v(-304.8, 292.1) * mm, "radius": 3.18 * mm});
            skCircle(sketch, "E2.11.3.0", {"center": v(-304.8, 266.7) * mm, "radius": 3.18 * mm});
            skCircle(sketch, "E2.11.4.0", {"center": v(-304.8, 241.3) * mm, "radius": 3.18 * mm});
            skCircle(sketch, "E2.11.5.0", {"center": v(-304.8, 215.9) * mm, "radius": 3.18 * mm});
            skCircle(sketch, "E2.11.6.0", {"center": v(-304.8, 190.5) * mm, "radius": 3.18 * mm});
            skCircle(sketch, "E2.11.7.0", {"center": v(-304.8, 165.1) * mm, "radius": 3.18 * mm});
            skCircle(sketch, "E2.11.8.0", {"center": v(-304.8, 139.7) * mm, "radius": 3.18 * mm});
            skCircle(sketch, "E2.11.9.0", {"center": v(-304.8, 114.3) * mm, "radius": 3.18 * mm});
            skCircle(sketch, "E2.11.10.0", {"center": v(-304.8, 88.9) * mm, "radius": 3.18 * mm});
            skCircle(sketch, "E2.11.11.0", {"center": v(-304.8, 63.5) * mm, "radius": 3.18 * mm});
            skCircle(sketch, "E2.11.12.0", {"center": v(-304.8, 38.1) * mm, "radius": 3.18 * mm});
            skCircle(sketch, "E2.11.13.0", {"center": v(-304.8, 12.7) * mm, "radius": 3.18 * mm});
            skCircle(sketch, "E2.11.14.0", {"center": v(-304.8, -12.7) * mm, "radius": 3.18 * mm});
            skCircle(sketch, "E2.11.15.0", {"center": v(-304.8, -38.1) * mm, "radius": 3.18 * mm});
            skCircle(sketch, "E2.11.16.0", {"center": v(-304.8, -63.5) * mm, "radius": 3.18 * mm});
            skCircle(sketch, "E2.11.17.0", {"center": v(-304.8, -88.9) * mm, "radius": 3.18 * mm});
            skCircle(sketch, "E2.11.18.0", {"center": v(-304.8, -114.3) * mm, "radius": 3.18 * mm});
            skCircle(sketch, "E2.11.19.0", {"center": v(-304.8, -139.7) * mm, "radius": 3.18 * mm});
            skCircle(sketch, "E2.11.20.0", {"center": v(-304.8, -165.1) * mm, "radius": 3.18 * mm});
            skCircle(sketch, "E2.11.21.0", {"center": v(-304.8, -190.5) * mm, "radius": 3.18 * mm});
            skCircle(sketch, "E2.11.22.0", {"center": v(-304.8, -215.9) * mm, "radius": 3.18 * mm});
            skCircle(sketch, "E2.11.23.0", {"center": v(-304.8, -241.3) * mm, "radius": 3.18 * mm});
            skCircle(sketch, "E2.11.24.0", {"center": v(-304.8, -266.7) * mm, "radius": 3.18 * mm});
            skCircle(sketch, "E2.11.25.0", {"center": v(-304.8, -292.1) * mm, "radius": 3.18 * mm});
            skCircle(sketch, "E2.11.26.0", {"center": v(-304.8, -317.5) * mm, "radius": 3.18 * mm});
            skCircle(sketch, "E2.11.27.0", {"center": v(-304.8, -342.9) * mm, "radius": 3.18 * mm});
            skCircle(sketch, "E2.12.0.0", {"center": v(-279.4, 342.9) * mm, "radius": 3.18 * mm});
            skCircle(sketch, "E2.12.1.0", {"center": v(-279.4, 317.5) * mm, "radius": 3.18 * mm});
            skCircle(sketch, "E2.12.2.0", {"center": v(-279.4, 292.1) * mm, "radius": 3.18 * mm});
            skCircle(sketch, "E2.12.3.0", {"center": v(-279.4, 266.7) * mm, "radius": 3.18 * mm});
            skCircle(sketch, "E2.12.4.0", {"center": v(-279.4, 241.3) * mm, "radius": 3.18 * mm});
            skCircle(sketch, "E2.12.5.0", {"center": v(-279.4, 215.9) * mm, "radius": 3.18 * mm});
            skCircle(sketch, "E2.12.6.0", {"center": v(-279.4, 190.5) * mm, "radius": 3.18 * mm});
            skCircle(sketch, "E2.12.7.0", {"center": v(-279.4, 165.1) * mm, "radius": 3.18 * mm});
            skCircle(sketch, "E2.12.8.0", {"center": v(-279.4, 139.7) * mm, "radius": 3.18 * mm});
            skCircle(sketch, "E2.12.9.0", {"center": v(-279.4, 114.3) * mm, "radius": 3.18 * mm});
            skCircle(sketch, "E2.12.10.0", {"center": v(-279.4, 88.9) * mm, "radius": 3.18 * mm});
            skCircle(sketch, "E2.12.11.0", {"center": v(-279.4, 63.5) * mm, "radius": 3.18 * mm});
            skCircle(sketch, "E2.12.12.0", {"center": v(-279.4, 38.1) * mm, "radius": 3.18 * mm});
            skCircle(sketch, "E2.12.13.0", {"center": v(-279.4, 12.7) * mm, "radius": 3.18 * mm});
            skCircle(sketch, "E2.12.14.0", {"center": v(-279.4, -12.7) * mm, "radius": 3.18 * mm});
            skCircle(sketch, "E2.12.15.0", {"center": v(-279.4, -38.1) * mm, "radius": 3.18 * mm});
            skCircle(sketch, "E2.12.16.0", {"center": v(-279.4, -63.5) * mm, "radius": 3.18 * mm});
            skCircle(sketch, "E2.12.17.0", {"center": v(-279.4, -88.9) * mm, "radius": 3.18 * mm});
            skCircle(sketch, "E2.12.18.0", {"center": v(-279.4, -114.3) * mm, "radius": 3.18 * mm});
            skCircle(sketch, "E2.12.19.0", {"center": v(-279.4, -139.7) * mm, "radius": 3.18 * mm});
            skCircle(sketch, "E2.12.20.0", {"center": v(-279.4, -165.1) * mm, "radius": 3.18 * mm});
            skCircle(sketch, "E2.12.21.0", {"center": v(-279.4, -190.5) * mm, "radius": 3.18 * mm});
            skCircle(sketch, "E2.12.22.0", {"center": v(-279.4, -215.9) * mm, "radius": 3.18 * mm});
            skCircle(sketch, "E2.12.23.0", {"center": v(-279.4, -241.3) * mm, "radius": 3.18 * mm});
            skCircle(sketch, "E2.12.24.0", {"center": v(-279.4, -266.7) * mm, "radius": 3.18 * mm});
            skCircle(sketch, "E2.12.25.0", {"center": v(-279.4, -292.1) * mm, "radius": 3.18 * mm});
            skCircle(sketch, "E2.12.26.0", {"center": v(-279.4, -317.5) * mm, "radius": 3.18 * mm});
            skCircle(sketch, "E2.12.27.0", {"center": v(-279.4, -342.9) * mm, "radius": 3.18 * mm});
            skCircle(sketch, "E2.13.0.0", {"center": v(-254, 342.9) * mm, "radius": 3.18 * mm});
            skCircle(sketch, "E2.13.1.0", {"center": v(-254, 317.5) * mm, "radius": 3.18 * mm});
            skCircle(sketch, "E2.13.2.0", {"center": v(-254, 292.1) * mm, "radius": 3.18 * mm});
            skCircle(sketch, "E2.13.3.0", {"center": v(-254, 266.7) * mm, "radius": 3.18 * mm});
            skCircle(sketch, "E2.13.4.0", {"center": v(-254, 241.3) * mm, "radius": 3.18 * mm});
            skCircle(sketch, "E2.13.5.0", {"center": v(-254, 215.9) * mm, "radius": 3.18 * mm});
            skCircle(sketch, "E2.13.6.0", {"center": v(-254, 190.5) * mm, "radius": 3.18 * mm});
            skCircle(sketch, "E2.13.7.0", {"center": v(-254, 165.1) * mm, "radius": 3.18 * mm});
            skCircle(sketch, "E2.13.8.0", {"center": v(-254, 139.7) * mm, "radius": 3.18 * mm});
            skCircle(sketch, "E2.13.9.0", {"center": v(-254, 114.3) * mm, "radius": 3.18 * mm});
            skCircle(sketch, "E2.13.10.0", {"center": v(-254, 88.9) * mm, "radius": 3.18 * mm});
            skCircle(sketch, "E2.13.11.0", {"center": v(-254, 63.5) * mm, "radius": 3.18 * mm});
            skCircle(sketch, "E2.13.12.0", {"center": v(-254, 38.1) * mm, "radius": 3.18 * mm});
            skCircle(sketch, "E2.13.13.0", {"center": v(-254, 12.7) * mm, "radius": 3.18 * mm});
            skCircle(sketch, "E2.13.14.0", {"center": v(-254, -12.7) * mm, "radius": 3.18 * mm});
            skCircle(sketch, "E2.13.15.0", {"center": v(-254, -38.1) * mm, "radius": 3.18 * mm});
            skCircle(sketch, "E2.13.16.0", {"center": v(-254, -63.5) * mm, "radius": 3.18 * mm});
            skCircle(sketch, "E2.13.17.0", {"center": v(-254, -88.9) * mm, "radius": 3.18 * mm});
            skCircle(sketch, "E2.13.18.0", {"center": v(-254, -114.3) * mm, "radius": 3.18 * mm});
            skCircle(sketch, "E2.13.19.0", {"center": v(-254, -139.7) * mm, "radius": 3.18 * mm});
            skCircle(sketch, "E2.13.20.0", {"center": v(-254, -165.1) * mm, "radius": 3.18 * mm});
            skCircle(sketch, "E2.13.21.0", {"center": v(-254, -190.5) * mm, "radius": 3.18 * mm});
            skCircle(sketch, "E2.13.22.0", {"center": v(-254, -215.9) * mm, "radius": 3.18 * mm});
            skCircle(sketch, "E2.13.23.0", {"center": v(-254, -241.3) * mm, "radius": 3.18 * mm});
            skCircle(sketch, "E2.13.24.0", {"center": v(-254, -266.7) * mm, "radius": 3.18 * mm});
            skCircle(sketch, "E2.13.25.0", {"center": v(-254, -292.1) * mm, "radius": 3.18 * mm});
            skCircle(sketch, "E2.13.26.0", {"center": v(-254, -317.5) * mm, "radius": 3.18 * mm});
            skCircle(sketch, "E2.13.27.0", {"center": v(-254, -342.9) * mm, "radius": 3.18 * mm});
            skCircle(sketch, "E2.14.0.0", {"center": v(-228.6, 342.9) * mm, "radius": 3.18 * mm});
            skCircle(sketch, "E2.14.1.0", {"center": v(-228.6, 317.5) * mm, "radius": 3.18 * mm});
            skCircle(sketch, "E2.14.2.0", {"center": v(-228.6, 292.1) * mm, "radius": 3.18 * mm});
            skCircle(sketch, "E2.14.3.0", {"center": v(-228.6, 266.7) * mm, "radius": 3.18 * mm});
            skCircle(sketch, "E2.14.4.0", {"center": v(-228.6, 241.3) * mm, "radius": 3.18 * mm});
            skCircle(sketch, "E2.14.5.0", {"center": v(-228.6, 215.9) * mm, "radius": 3.18 * mm});
            skCircle(sketch, "E2.14.6.0", {"center": v(-228.6, 190.5) * mm, "radius": 3.18 * mm});
            skCircle(sketch, "E2.14.7.0", {"center": v(-228.6, 165.1) * mm, "radius": 3.18 * mm});
            skCircle(sketch, "E2.14.8.0", {"center": v(-228.6, 139.7) * mm, "radius": 3.18 * mm});
            skCircle(sketch, "E2.14.9.0", {"center": v(-228.6, 114.3) * mm, "radius": 3.18 * mm});
            skCircle(sketch, "E2.14.10.0", {"center": v(-228.6, 88.9) * mm, "radius": 3.18 * mm});
            skCircle(sketch, "E2.14.11.0", {"center": v(-228.6, 63.5) * mm, "radius": 3.18 * mm});
            skCircle(sketch, "E2.14.12.0", {"center": v(-228.6, 38.1) * mm, "radius": 3.18 * mm});
            skCircle(sketch, "E2.14.13.0", {"center": v(-228.6, 12.7) * mm, "radius": 3.18 * mm});
            skCircle(sketch, "E2.14.14.0", {"center": v(-228.6, -12.7) * mm, "radius": 3.18 * mm});
            skCircle(sketch, "E2.14.15.0", {"center": v(-228.6, -38.1) * mm, "radius": 3.18 * mm});
            skCircle(sketch, "E2.14.16.0", {"center": v(-228.6, -63.5) * mm, "radius": 3.18 * mm});
            skCircle(sketch, "E2.14.17.0", {"center": v(-228.6, -88.9) * mm, "radius": 3.18 * mm});
            skCircle(sketch, "E2.14.18.0", {"center": v(-228.6, -114.3) * mm, "radius": 3.18 * mm});
            skCircle(sketch, "E2.14.19.0", {"center": v(-228.6, -139.7) * mm, "radius": 3.18 * mm});
            skCircle(sketch, "E2.14.20.0", {"center": v(-228.6, -165.1) * mm, "radius": 3.18 * mm});
            skCircle(sketch, "E2.14.21.0", {"center": v(-228.6, -190.5) * mm, "radius": 3.18 * mm});
            skCircle(sketch, "E2.14.22.0", {"center": v(-228.6, -215.9) * mm, "radius": 3.18 * mm});
            skCircle(sketch, "E2.14.23.0", {"center": v(-228.6, -241.3) * mm, "radius": 3.18 * mm});
            skCircle(sketch, "E2.14.24.0", {"center": v(-228.6, -266.7) * mm, "radius": 3.18 * mm});
            skCircle(sketch, "E2.14.25.0", {"center": v(-228.6, -292.1) * mm, "radius": 3.18 * mm});
            skCircle(sketch, "E2.14.26.0", {"center": v(-228.6, -317.5) * mm, "radius": 3.18 * mm});
            skCircle(sketch, "E2.14.27.0", {"center": v(-228.6, -342.9) * mm, "radius": 3.18 * mm});
            skCircle(sketch, "E2.15.0.0", {"center": v(-203.2, 342.9) * mm, "radius": 3.18 * mm});
            skCircle(sketch, "E2.15.1.0", {"center": v(-203.2, 317.5) * mm, "radius": 3.18 * mm});
            skCircle(sketch, "E2.15.2.0", {"center": v(-203.2, 292.1) * mm, "radius": 3.18 * mm});
            skCircle(sketch, "E2.15.3.0", {"center": v(-203.2, 266.7) * mm, "radius": 3.18 * mm});
            skCircle(sketch, "E2.15.4.0", {"center": v(-203.2, 241.3) * mm, "radius": 3.18 * mm});
            skCircle(sketch, "E2.15.5.0", {"center": v(-203.2, 215.9) * mm, "radius": 3.18 * mm});
            skCircle(sketch, "E2.15.6.0", {"center": v(-203.2, 190.5) * mm, "radius": 3.18 * mm});
            skCircle(sketch, "E2.15.7.0", {"center": v(-203.2, 165.1) * mm, "radius": 3.18 * mm});
            skCircle(sketch, "E2.15.8.0", {"center": v(-203.2, 139.7) * mm, "radius": 3.18 * mm});
            skCircle(sketch, "E2.15.9.0", {"center": v(-203.2, 114.3) * mm, "radius": 3.18 * mm});
            skCircle(sketch, "E2.15.10.0", {"center": v(-203.2, 88.9) * mm, "radius": 3.18 * mm});
            skCircle(sketch, "E2.15.11.0", {"center": v(-203.2, 63.5) * mm, "radius": 3.18 * mm});
            skCircle(sketch, "E2.15.12.0", {"center": v(-203.2, 38.1) * mm, "radius": 3.18 * mm});
            skCircle(sketch, "E2.15.13.0", {"center": v(-203.2, 12.7) * mm, "radius": 3.18 * mm});
            skCircle(sketch, "E2.15.14.0", {"center": v(-203.2, -12.7) * mm, "radius": 3.18 * mm});
            skCircle(sketch, "E2.15.15.0", {"center": v(-203.2, -38.1) * mm, "radius": 3.18 * mm});
            skCircle(sketch, "E2.15.16.0", {"center": v(-203.2, -63.5) * mm, "radius": 3.18 * mm});
            skCircle(sketch, "E2.15.17.0", {"center": v(-203.2, -88.9) * mm, "radius": 3.18 * mm});
            skCircle(sketch, "E2.15.18.0", {"center": v(-203.2, -114.3) * mm, "radius": 3.18 * mm});
            skCircle(sketch, "E2.15.19.0", {"center": v(-203.2, -139.7) * mm, "radius": 3.18 * mm});
            skCircle(sketch, "E2.15.20.0", {"center": v(-203.2, -165.1) * mm, "radius": 3.18 * mm});
            skCircle(sketch, "E2.15.21.0", {"center": v(-203.2, -190.5) * mm, "radius": 3.18 * mm});
            skCircle(sketch, "E2.15.22.0", {"center": v(-203.2, -215.9) * mm, "radius": 3.18 * mm});
            skCircle(sketch, "E2.15.23.0", {"center": v(-203.2, -241.3) * mm, "radius": 3.18 * mm});
            skCircle(sketch, "E2.15.24.0", {"center": v(-203.2, -266.7) * mm, "radius": 3.18 * mm});
            skCircle(sketch, "E2.15.25.0", {"center": v(-203.2, -292.1) * mm, "radius": 3.18 * mm});
            skCircle(sketch, "E2.15.26.0", {"center": v(-203.2, -317.5) * mm, "radius": 3.18 * mm});
            skCircle(sketch, "E2.15.27.0", {"center": v(-203.2, -342.9) * mm, "radius": 3.18 * mm});
            skCircle(sketch, "E2.16.0.0", {"center": v(-177.8, 342.9) * mm, "radius": 3.18 * mm});
            skCircle(sketch, "E2.16.1.0", {"center": v(-177.8, 317.5) * mm, "radius": 3.18 * mm});
            skCircle(sketch, "E2.16.2.0", {"center": v(-177.8, 292.1) * mm, "radius": 3.18 * mm});
            skCircle(sketch, "E2.16.3.0", {"center": v(-177.8, 266.7) * mm, "radius": 3.18 * mm});
            skCircle(sketch, "E2.16.4.0", {"center": v(-177.8, 241.3) * mm, "radius": 3.18 * mm});
            skCircle(sketch, "E2.16.5.0", {"center": v(-177.8, 215.9) * mm, "radius": 3.18 * mm});
            skCircle(sketch, "E2.16.6.0", {"center": v(-177.8, 190.5) * mm, "radius": 3.18 * mm});
            skCircle(sketch, "E2.16.7.0", {"center": v(-177.8, 165.1) * mm, "radius": 3.18 * mm});
            skCircle(sketch, "E2.16.8.0", {"center": v(-177.8, 139.7) * mm, "radius": 3.18 * mm});
            skCircle(sketch, "E2.16.9.0", {"center": v(-177.8, 114.3) * mm, "radius": 3.18 * mm});
            skCircle(sketch, "E2.16.10.0", {"center": v(-177.8, 88.9) * mm, "radius": 3.18 * mm});
            skCircle(sketch, "E2.16.11.0", {"center": v(-177.8, 63.5) * mm, "radius": 3.18 * mm});
            skCircle(sketch, "E2.16.12.0", {"center": v(-177.8, 38.1) * mm, "radius": 3.18 * mm});
            skCircle(sketch, "E2.16.13.0", {"center": v(-177.8, 12.7) * mm, "radius": 3.18 * mm});
            skCircle(sketch, "E2.16.14.0", {"center": v(-177.8, -12.7) * mm, "radius": 3.18 * mm});
            skCircle(sketch, "E2.16.15.0", {"center": v(-177.8, -38.1) * mm, "radius": 3.18 * mm});
            skCircle(sketch, "E2.16.16.0", {"center": v(-177.8, -63.5) * mm, "radius": 3.18 * mm});
            skCircle(sketch, "E2.16.17.0", {"center": v(-177.8, -88.9) * mm, "radius": 3.18 * mm});
            skCircle(sketch, "E2.16.18.0", {"center": v(-177.8, -114.3) * mm, "radius": 3.18 * mm});
            skCircle(sketch, "E2.16.19.0", {"center": v(-177.8, -139.7) * mm, "radius": 3.18 * mm});
            skCircle(sketch, "E2.16.20.0", {"center": v(-177.8, -165.1) * mm, "radius": 3.18 * mm});
            skCircle(sketch, "E2.16.21.0", {"center": v(-177.8, -190.5) * mm, "radius": 3.18 * mm});
            skCircle(sketch, "E2.16.22.0", {"center": v(-177.8, -215.9) * mm, "radius": 3.18 * mm});
            skCircle(sketch, "E2.16.23.0", {"center": v(-177.8, -241.3) * mm, "radius": 3.18 * mm});
            skCircle(sketch, "E2.16.24.0", {"center": v(-177.8, -266.7) * mm, "radius": 3.18 * mm});
            skCircle(sketch, "E2.16.25.0", {"center": v(-177.8, -292.1) * mm, "radius": 3.18 * mm});
            skCircle(sketch, "E2.16.26.0", {"center": v(-177.8, -317.5) * mm, "radius": 3.18 * mm});
            skCircle(sketch, "E2.16.27.0", {"center": v(-177.8, -342.9) * mm, "radius": 3.18 * mm});
            skCircle(sketch, "E2.17.0.0", {"center": v(-152.4, 342.9) * mm, "radius": 3.18 * mm});
            skCircle(sketch, "E2.17.1.0", {"center": v(-152.4, 317.5) * mm, "radius": 3.18 * mm});
            skCircle(sketch, "E2.17.2.0", {"center": v(-152.4, 292.1) * mm, "radius": 3.18 * mm});
            skCircle(sketch, "E2.17.3.0", {"center": v(-152.4, 266.7) * mm, "radius": 3.18 * mm});
            skCircle(sketch, "E2.17.4.0", {"center": v(-152.4, 241.3) * mm, "radius": 3.18 * mm});
            skCircle(sketch, "E2.17.5.0", {"center": v(-152.4, 215.9) * mm, "radius": 3.18 * mm});
            skCircle(sketch, "E2.17.6.0", {"center": v(-152.4, 190.5) * mm, "radius": 3.18 * mm});
            skCircle(sketch, "E2.17.7.0", {"center": v(-152.4, 165.1) * mm, "radius": 3.18 * mm});
            skCircle(sketch, "E2.17.8.0", {"center": v(-152.4, 139.7) * mm, "radius": 3.18 * mm});
            skCircle(sketch, "E2.17.9.0", {"center": v(-152.4, 114.3) * mm, "radius": 3.18 * mm});
            skCircle(sketch, "E2.17.10.0", {"center": v(-152.4, 88.9) * mm, "radius": 3.18 * mm});
            skCircle(sketch, "E2.17.11.0", {"center": v(-152.4, 63.5) * mm, "radius": 3.18 * mm});
            skCircle(sketch, "E2.17.12.0", {"center": v(-152.4, 38.1) * mm, "radius": 3.18 * mm});
            skCircle(sketch, "E2.17.13.0", {"center": v(-152.4, 12.7) * mm, "radius": 3.18 * mm});
            skCircle(sketch, "E2.17.14.0", {"center": v(-152.4, -12.7) * mm, "radius": 3.18 * mm});
            skCircle(sketch, "E2.17.15.0", {"center": v(-152.4, -38.1) * mm, "radius": 3.18 * mm});
            skCircle(sketch, "E2.17.16.0", {"center": v(-152.4, -63.5) * mm, "radius": 3.18 * mm});
            skCircle(sketch, "E2.17.17.0", {"center": v(-152.4, -88.9) * mm, "radius": 3.18 * mm});
            skCircle(sketch, "E2.17.18.0", {"center": v(-152.4, -114.3) * mm, "radius": 3.18 * mm});
            skCircle(sketch, "E2.17.19.0", {"center": v(-152.4, -139.7) * mm, "radius": 3.18 * mm});
            skCircle(sketch, "E2.17.20.0", {"center": v(-152.4, -165.1) * mm, "radius": 3.18 * mm});
            skCircle(sketch, "E2.17.21.0", {"center": v(-152.4, -190.5) * mm, "radius": 3.18 * mm});
            skCircle(sketch, "E2.17.22.0", {"center": v(-152.4, -215.9) * mm, "radius": 3.18 * mm});
            skCircle(sketch, "E2.17.23.0", {"center": v(-152.4, -241.3) * mm, "radius": 3.18 * mm});
            skCircle(sketch, "E2.17.24.0", {"center": v(-152.4, -266.7) * mm, "radius": 3.18 * mm});
            skCircle(sketch, "E2.17.25.0", {"center": v(-152.4, -292.1) * mm, "radius": 3.18 * mm});
            skCircle(sketch, "E2.17.26.0", {"center": v(-152.4, -317.5) * mm, "radius": 3.18 * mm});
            skCircle(sketch, "E2.17.27.0", {"center": v(-152.4, -342.9) * mm, "radius": 3.18 * mm});
            skCircle(sketch, "E2.18.0.0", {"center": v(-127, 342.9) * mm, "radius": 3.18 * mm});
            skCircle(sketch, "E2.18.1.0", {"center": v(-127, 317.5) * mm, "radius": 3.18 * mm});
            skCircle(sketch, "E2.18.2.0", {"center": v(-127, 292.1) * mm, "radius": 3.18 * mm});
            skCircle(sketch, "E2.18.3.0", {"center": v(-127, 266.7) * mm, "radius": 3.18 * mm});
            skCircle(sketch, "E2.18.4.0", {"center": v(-127, 241.3) * mm, "radius": 3.18 * mm});
            skCircle(sketch, "E2.18.5.0", {"center": v(-127, 215.9) * mm, "radius": 3.18 * mm});
            skCircle(sketch, "E2.18.6.0", {"center": v(-127, 190.5) * mm, "radius": 3.18 * mm});
            skCircle(sketch, "E2.18.7.0", {"center": v(-127, 165.1) * mm, "radius": 3.18 * mm});
            skCircle(sketch, "E2.18.8.0", {"center": v(-127, 139.7) * mm, "radius": 3.18 * mm});
            skCircle(sketch, "E2.18.9.0", {"center": v(-127, 114.3) * mm, "radius": 3.18 * mm});
            skCircle(sketch, "E2.18.10.0", {"center": v(-127, 88.9) * mm, "radius": 3.18 * mm});
            skCircle(sketch, "E2.18.11.0", {"center": v(-127, 63.5) * mm, "radius": 3.18 * mm});
            skCircle(sketch, "E2.18.12.0", {"center": v(-127, 38.1) * mm, "radius": 3.18 * mm});
            skCircle(sketch, "E2.18.13.0", {"center": v(-127, 12.7) * mm, "radius": 3.18 * mm});
            skCircle(sketch, "E2.18.14.0", {"center": v(-127, -12.7) * mm, "radius": 3.18 * mm});
            skCircle(sketch, "E2.18.15.0", {"center": v(-127, -38.1) * mm, "radius": 3.18 * mm});
            skCircle(sketch, "E2.18.16.0", {"center": v(-127, -63.5) * mm, "radius": 3.18 * mm});
            skCircle(sketch, "E2.18.17.0", {"center": v(-127, -88.9) * mm, "radius": 3.18 * mm});
            skCircle(sketch, "E2.18.18.0", {"center": v(-127, -114.3) * mm, "radius": 3.18 * mm});
            skCircle(sketch, "E2.18.19.0", {"center": v(-127, -139.7) * mm, "radius": 3.18 * mm});
            skCircle(sketch, "E2.18.20.0", {"center": v(-127, -165.1) * mm, "radius": 3.18 * mm});
            skCircle(sketch, "E2.18.21.0", {"center": v(-127, -190.5) * mm, "radius": 3.18 * mm});
            skCircle(sketch, "E2.18.22.0", {"center": v(-127, -215.9) * mm, "radius": 3.18 * mm});
            skCircle(sketch, "E2.18.23.0", {"center": v(-127, -241.3) * mm, "radius": 3.18 * mm});
            skCircle(sketch, "E2.18.24.0", {"center": v(-127, -266.7) * mm, "radius": 3.18 * mm});
            skCircle(sketch, "E2.18.25.0", {"center": v(-127, -292.1) * mm, "radius": 3.18 * mm});
            skCircle(sketch, "E2.18.26.0", {"center": v(-127, -317.5) * mm, "radius": 3.18 * mm});
            skCircle(sketch, "E2.18.27.0", {"center": v(-127, -342.9) * mm, "radius": 3.18 * mm});
            skCircle(sketch, "E2.19.0.0", {"center": v(-101.6, 342.9) * mm, "radius": 3.18 * mm});
            skCircle(sketch, "E2.19.1.0", {"center": v(-101.6, 317.5) * mm, "radius": 3.18 * mm});
            skCircle(sketch, "E2.19.2.0", {"center": v(-101.6, 292.1) * mm, "radius": 3.18 * mm});
            skCircle(sketch, "E2.19.3.0", {"center": v(-101.6, 266.7) * mm, "radius": 3.18 * mm});
            skCircle(sketch, "E2.19.4.0", {"center": v(-101.6, 241.3) * mm, "radius": 3.18 * mm});
            skCircle(sketch, "E2.19.5.0", {"center": v(-101.6, 215.9) * mm, "radius": 3.18 * mm});
            skCircle(sketch, "E2.19.6.0", {"center": v(-101.6, 190.5) * mm, "radius": 3.18 * mm});
            skCircle(sketch, "E2.19.7.0", {"center": v(-101.6, 165.1) * mm, "radius": 3.18 * mm});
            skCircle(sketch, "E2.19.8.0", {"center": v(-101.6, 139.7) * mm, "radius": 3.18 * mm});
            skCircle(sketch, "E2.19.9.0", {"center": v(-101.6, 114.3) * mm, "radius": 3.18 * mm});
            skCircle(sketch, "E2.19.10.0", {"center": v(-101.6, 88.9) * mm, "radius": 3.18 * mm});
            skCircle(sketch, "E2.19.11.0", {"center": v(-101.6, 63.5) * mm, "radius": 3.18 * mm});
            skCircle(sketch, "E2.19.12.0", {"center": v(-101.6, 38.1) * mm, "radius": 3.18 * mm});
            skCircle(sketch, "E2.19.13.0", {"center": v(-101.6, 12.7) * mm, "radius": 3.18 * mm});
            skCircle(sketch, "E2.19.14.0", {"center": v(-101.6, -12.7) * mm, "radius": 3.18 * mm});
            skCircle(sketch, "E2.19.15.0", {"center": v(-101.6, -38.1) * mm, "radius": 3.18 * mm});
            skCircle(sketch, "E2.19.16.0", {"center": v(-101.6, -63.5) * mm, "radius": 3.18 * mm});
            skCircle(sketch, "E2.19.17.0", {"center": v(-101.6, -88.9) * mm, "radius": 3.18 * mm});
            skCircle(sketch, "E2.19.18.0", {"center": v(-101.6, -114.3) * mm, "radius": 3.18 * mm});
            skCircle(sketch, "E2.19.19.0", {"center": v(-101.6, -139.7) * mm, "radius": 3.18 * mm});
            skCircle(sketch, "E2.19.20.0", {"center": v(-101.6, -165.1) * mm, "radius": 3.18 * mm});
            skCircle(sketch, "E2.19.21.0", {"center": v(-101.6, -190.5) * mm, "radius": 3.18 * mm});
            skCircle(sketch, "E2.19.22.0", {"center": v(-101.6, -215.9) * mm, "radius": 3.18 * mm});
            skCircle(sketch, "E2.19.23.0", {"center": v(-101.6, -241.3) * mm, "radius": 3.18 * mm});
            skCircle(sketch, "E2.19.24.0", {"center": v(-101.6, -266.7) * mm, "radius": 3.18 * mm});
            skCircle(sketch, "E2.19.25.0", {"center": v(-101.6, -292.1) * mm, "radius": 3.18 * mm});
            skCircle(sketch, "E2.19.26.0", {"center": v(-101.6, -317.5) * mm, "radius": 3.18 * mm});
            skCircle(sketch, "E2.19.27.0", {"center": v(-101.6, -342.9) * mm, "radius": 3.18 * mm});
            skCircle(sketch, "E2.20.0.0", {"center": v(-76.2, 342.9) * mm, "radius": 3.18 * mm});
            skCircle(sketch, "E2.20.1.0", {"center": v(-76.2, 317.5) * mm, "radius": 3.18 * mm});
            skCircle(sketch, "E2.20.2.0", {"center": v(-76.2, 292.1) * mm, "radius": 3.18 * mm});
            skCircle(sketch, "E2.20.3.0", {"center": v(-76.2, 266.7) * mm, "radius": 3.18 * mm});
            skCircle(sketch, "E2.20.4.0", {"center": v(-76.2, 241.3) * mm, "radius": 3.18 * mm});
            skCircle(sketch, "E2.20.5.0", {"center": v(-76.2, 215.9) * mm, "radius": 3.18 * mm});
            skCircle(sketch, "E2.20.6.0", {"center": v(-76.2, 190.5) * mm, "radius": 3.18 * mm});
            skCircle(sketch, "E2.20.7.0", {"center": v(-76.2, 165.1) * mm, "radius": 3.18 * mm});
            skCircle(sketch, "E2.20.8.0", {"center": v(-76.2, 139.7) * mm, "radius": 3.18 * mm});
            skCircle(sketch, "E2.20.9.0", {"center": v(-76.2, 114.3) * mm, "radius": 3.18 * mm});
            skCircle(sketch, "E2.20.10.0", {"center": v(-76.2, 88.9) * mm, "radius": 3.18 * mm});
            skCircle(sketch, "E2.20.11.0", {"center": v(-76.2, 63.5) * mm, "radius": 3.18 * mm});
            skCircle(sketch, "E2.20.12.0", {"center": v(-76.2, 38.1) * mm, "radius": 3.18 * mm});
            skCircle(sketch, "E2.20.13.0", {"center": v(-76.2, 12.7) * mm, "radius": 3.18 * mm});
            skCircle(sketch, "E2.20.14.0", {"center": v(-76.2, -12.7) * mm, "radius": 3.18 * mm});
            skCircle(sketch, "E2.20.15.0", {"center": v(-76.2, -38.1) * mm, "radius": 3.18 * mm});
            skCircle(sketch, "E2.20.16.0", {"center": v(-76.2, -63.5) * mm, "radius": 3.18 * mm});
            skCircle(sketch, "E2.20.17.0", {"center": v(-76.2, -88.9) * mm, "radius": 3.18 * mm});
            skCircle(sketch, "E2.20.18.0", {"center": v(-76.2, -114.3) * mm, "radius": 3.18 * mm});
            skCircle(sketch, "E2.20.19.0", {"center": v(-76.2, -139.7) * mm, "radius": 3.18 * mm});
            skCircle(sketch, "E2.20.20.0", {"center": v(-76.2, -165.1) * mm, "radius": 3.18 * mm});
            skCircle(sketch, "E2.20.21.0", {"center": v(-76.2, -190.5) * mm, "radius": 3.18 * mm});
            skCircle(sketch, "E2.20.22.0", {"center": v(-76.2, -215.9) * mm, "radius": 3.18 * mm});
            skCircle(sketch, "E2.20.23.0", {"center": v(-76.2, -241.3) * mm, "radius": 3.18 * mm});
            skCircle(sketch, "E2.20.24.0", {"center": v(-76.2, -266.7) * mm, "radius": 3.18 * mm});
            skCircle(sketch, "E2.20.25.0", {"center": v(-76.2, -292.1) * mm, "radius": 3.18 * mm});
            skCircle(sketch, "E2.20.26.0", {"center": v(-76.2, -317.5) * mm, "radius": 3.18 * mm});
            skCircle(sketch, "E2.20.27.0", {"center": v(-76.2, -342.9) * mm, "radius": 3.18 * mm});
            skCircle(sketch, "E2.21.0.0", {"center": v(-50.8, 342.9) * mm, "radius": 3.18 * mm});
            skCircle(sketch, "E2.21.1.0", {"center": v(-50.8, 317.5) * mm, "radius": 3.18 * mm});
            skCircle(sketch, "E2.21.2.0", {"center": v(-50.8, 292.1) * mm, "radius": 3.18 * mm});
            skCircle(sketch, "E2.21.3.0", {"center": v(-50.8, 266.7) * mm, "radius": 3.18 * mm});
            skCircle(sketch, "E2.21.4.0", {"center": v(-50.8, 241.3) * mm, "radius": 3.18 * mm});
            skCircle(sketch, "E2.21.5.0", {"center": v(-50.8, 215.9) * mm, "radius": 3.18 * mm});
            skCircle(sketch, "E2.21.6.0", {"center": v(-50.8, 190.5) * mm, "radius": 3.18 * mm});
            skCircle(sketch, "E2.21.7.0", {"center": v(-50.8, 165.1) * mm, "radius": 3.18 * mm});
            skCircle(sketch, "E2.21.8.0", {"center": v(-50.8, 139.7) * mm, "radius": 3.18 * mm});
            skCircle(sketch, "E2.21.9.0", {"center": v(-50.8, 114.3) * mm, "radius": 3.18 * mm});
            skCircle(sketch, "E2.21.10.0", {"center": v(-50.8, 88.9) * mm, "radius": 3.18 * mm});
            skCircle(sketch, "E2.21.11.0", {"center": v(-50.8, 63.5) * mm, "radius": 3.18 * mm});
            skCircle(sketch, "E2.21.12.0", {"center": v(-50.8, 38.1) * mm, "radius": 3.18 * mm});
            skCircle(sketch, "E2.21.13.0", {"center": v(-50.8, 12.7) * mm, "radius": 3.18 * mm});
            skCircle(sketch, "E2.21.14.0", {"center": v(-50.8, -12.7) * mm, "radius": 3.18 * mm});
            skCircle(sketch, "E2.21.15.0", {"center": v(-50.8, -38.1) * mm, "radius": 3.18 * mm});
            skCircle(sketch, "E2.21.16.0", {"center": v(-50.8, -63.5) * mm, "radius": 3.18 * mm});
            skCircle(sketch, "E2.21.17.0", {"center": v(-50.8, -88.9) * mm, "radius": 3.18 * mm});
            skCircle(sketch, "E2.21.18.0", {"center": v(-50.8, -114.3) * mm, "radius": 3.18 * mm});
            skCircle(sketch, "E2.21.19.0", {"center": v(-50.8, -139.7) * mm, "radius": 3.18 * mm});
            skCircle(sketch, "E2.21.20.0", {"center": v(-50.8, -165.1) * mm, "radius": 3.18 * mm});
            skCircle(sketch, "E2.21.21.0", {"center": v(-50.8, -190.5) * mm, "radius": 3.18 * mm});
            skCircle(sketch, "E2.21.22.0", {"center": v(-50.8, -215.9) * mm, "radius": 3.18 * mm});
            skCircle(sketch, "E2.21.23.0", {"center": v(-50.8, -241.3) * mm, "radius": 3.18 * mm});
            skCircle(sketch, "E2.21.24.0", {"center": v(-50.8, -266.7) * mm, "radius": 3.18 * mm});
            skCircle(sketch, "E2.21.25.0", {"center": v(-50.8, -292.1) * mm, "radius": 3.18 * mm});
            skCircle(sketch, "E2.21.26.0", {"center": v(-50.8, -317.5) * mm, "radius": 3.18 * mm});
            skCircle(sketch, "E2.21.27.0", {"center": v(-50.8, -342.9) * mm, "radius": 3.18 * mm});
            skCircle(sketch, "E2.22.0.0", {"center": v(-25.4, 342.9) * mm, "radius": 3.18 * mm});
            skCircle(sketch, "E2.22.1.0", {"center": v(-25.4, 317.5) * mm, "radius": 3.18 * mm});
            skCircle(sketch, "E2.22.2.0", {"center": v(-25.4, 292.1) * mm, "radius": 3.18 * mm});
            skCircle(sketch, "E2.22.3.0", {"center": v(-25.4, 266.7) * mm, "radius": 3.18 * mm});
            skCircle(sketch, "E2.22.4.0", {"center": v(-25.4, 241.3) * mm, "radius": 3.18 * mm});
            skCircle(sketch, "E2.22.5.0", {"center": v(-25.4, 215.9) * mm, "radius": 3.18 * mm});
            skCircle(sketch, "E2.22.6.0", {"center": v(-25.4, 190.5) * mm, "radius": 3.18 * mm});
            skCircle(sketch, "E2.22.7.0", {"center": v(-25.4, 165.1) * mm, "radius": 3.18 * mm});
            skCircle(sketch, "E2.22.8.0", {"center": v(-25.4, 139.7) * mm, "radius": 3.18 * mm});
            skCircle(sketch, "E2.22.9.0", {"center": v(-25.4, 114.3) * mm, "radius": 3.18 * mm});
            skCircle(sketch, "E2.22.10.0", {"center": v(-25.4, 88.9) * mm, "radius": 3.18 * mm});
            skCircle(sketch, "E2.22.11.0", {"center": v(-25.4, 63.5) * mm, "radius": 3.18 * mm});
            skCircle(sketch, "E2.22.12.0", {"center": v(-25.4, 38.1) * mm, "radius": 3.18 * mm});
            skCircle(sketch, "E2.22.13.0", {"center": v(-25.4, 12.7) * mm, "radius": 3.18 * mm});
            skCircle(sketch, "E2.22.14.0", {"center": v(-25.4, -12.7) * mm, "radius": 3.18 * mm});
            skCircle(sketch, "E2.22.15.0", {"center": v(-25.4, -38.1) * mm, "radius": 3.18 * mm});
            skCircle(sketch, "E2.22.16.0", {"center": v(-25.4, -63.5) * mm, "radius": 3.18 * mm});
            skCircle(sketch, "E2.22.17.0", {"center": v(-25.4, -88.9) * mm, "radius": 3.18 * mm});
            skCircle(sketch, "E2.22.18.0", {"center": v(-25.4, -114.3) * mm, "radius": 3.18 * mm});
            skCircle(sketch, "E2.22.19.0", {"center": v(-25.4, -139.7) * mm, "radius": 3.18 * mm});
            skCircle(sketch, "E2.22.20.0", {"center": v(-25.4, -165.1) * mm, "radius": 3.18 * mm});
            skCircle(sketch, "E2.22.21.0", {"center": v(-25.4, -190.5) * mm, "radius": 3.18 * mm});
            skCircle(sketch, "E2.22.22.0", {"center": v(-25.4, -215.9) * mm, "radius": 3.18 * mm});
            skCircle(sketch, "E2.22.23.0", {"center": v(-25.4, -241.3) * mm, "radius": 3.18 * mm});
            skCircle(sketch, "E2.22.24.0", {"center": v(-25.4, -266.7) * mm, "radius": 3.18 * mm});
            skCircle(sketch, "E2.22.25.0", {"center": v(-25.4, -292.1) * mm, "radius": 3.18 * mm});
            skCircle(sketch, "E2.22.26.0", {"center": v(-25.4, -317.5) * mm, "radius": 3.18 * mm});
            skCircle(sketch, "E2.22.27.0", {"center": v(-25.4, -342.9) * mm, "radius": 3.18 * mm});
            skCircle(sketch, "E2.23.0.0", {"center": v(0, 342.9) * mm, "radius": 3.18 * mm});
            skCircle(sketch, "E2.23.1.0", {"center": v(0, 317.5) * mm, "radius": 3.18 * mm});
            skCircle(sketch, "E2.23.2.0", {"center": v(0, 292.1) * mm, "radius": 3.18 * mm});
            skCircle(sketch, "E2.23.3.0", {"center": v(0, 266.7) * mm, "radius": 3.18 * mm});
            skCircle(sketch, "E2.23.4.0", {"center": v(0, 241.3) * mm, "radius": 3.18 * mm});
            skCircle(sketch, "E2.23.5.0", {"center": v(0, 215.9) * mm, "radius": 3.18 * mm});
            skCircle(sketch, "E2.23.6.0", {"center": v(0, 190.5) * mm, "radius": 3.18 * mm});
            skCircle(sketch, "E2.23.7.0", {"center": v(0, 165.1) * mm, "radius": 3.18 * mm});
            skCircle(sketch, "E2.23.8.0", {"center": v(0, 139.7) * mm, "radius": 3.18 * mm});
            skCircle(sketch, "E2.23.9.0", {"center": v(0, 114.3) * mm, "radius": 3.18 * mm});
            skCircle(sketch, "E2.23.10.0", {"center": v(0, 88.9) * mm, "radius": 3.18 * mm});
            skCircle(sketch, "E2.23.11.0", {"center": v(0, 63.5) * mm, "radius": 3.18 * mm});
            skCircle(sketch, "E2.23.12.0", {"center": v(0, 38.1) * mm, "radius": 3.18 * mm});
            skCircle(sketch, "E2.23.13.0", {"center": v(0, 12.7) * mm, "radius": 3.18 * mm});
            skCircle(sketch, "E2.23.14.0", {"center": v(0, -12.7) * mm, "radius": 3.18 * mm});
            skCircle(sketch, "E2.23.15.0", {"center": v(0, -38.1) * mm, "radius": 3.18 * mm});
            skCircle(sketch, "E2.23.16.0", {"center": v(0, -63.5) * mm, "radius": 3.18 * mm});
            skCircle(sketch, "E2.23.17.0", {"center": v(0, -88.9) * mm, "radius": 3.18 * mm});
            skCircle(sketch, "E2.23.18.0", {"center": v(0, -114.3) * mm, "radius": 3.18 * mm});
            skCircle(sketch, "E2.23.19.0", {"center": v(0, -139.7) * mm, "radius": 3.18 * mm});
            skCircle(sketch, "E2.23.20.0", {"center": v(0, -165.1) * mm, "radius": 3.18 * mm});
            skCircle(sketch, "E2.23.21.0", {"center": v(0, -190.5) * mm, "radius": 3.18 * mm});
            skCircle(sketch, "E2.23.22.0", {"center": v(0, -215.9) * mm, "radius": 3.18 * mm});
            skCircle(sketch, "E2.23.23.0", {"center": v(0, -241.3) * mm, "radius": 3.18 * mm});
            skCircle(sketch, "E2.23.24.0", {"center": v(0, -266.7) * mm, "radius": 3.18 * mm});
            skCircle(sketch, "E2.23.25.0", {"center": v(0, -292.1) * mm, "radius": 3.18 * mm});
            skCircle(sketch, "E2.23.26.0", {"center": v(0, -317.5) * mm, "radius": 3.18 * mm});
            skCircle(sketch, "E2.23.27.0", {"center": v(0, -342.9) * mm, "radius": 3.18 * mm});
            skCircle(sketch, "E2.24.0.0", {"center": v(25.4, 342.9) * mm, "radius": 3.18 * mm});
            skCircle(sketch, "E2.24.1.0", {"center": v(25.4, 317.5) * mm, "radius": 3.18 * mm});
            skCircle(sketch, "E2.24.2.0", {"center": v(25.4, 292.1) * mm, "radius": 3.18 * mm});
            skCircle(sketch, "E2.24.3.0", {"center": v(25.4, 266.7) * mm, "radius": 3.18 * mm});
            skCircle(sketch, "E2.24.4.0", {"center": v(25.4, 241.3) * mm, "radius": 3.18 * mm});
            skCircle(sketch, "E2.24.5.0", {"center": v(25.4, 215.9) * mm, "radius": 3.18 * mm});
            skCircle(sketch, "E2.24.6.0", {"center": v(25.4, 190.5) * mm, "radius": 3.18 * mm});
            skCircle(sketch, "E2.24.7.0", {"center": v(25.4, 165.1) * mm, "radius": 3.18 * mm});
            skCircle(sketch, "E2.24.8.0", {"center": v(25.4, 139.7) * mm, "radius": 3.18 * mm});
            skCircle(sketch, "E2.24.9.0", {"center": v(25.4, 114.3) * mm, "radius": 3.18 * mm});
            skCircle(sketch, "E2.24.10.0", {"center": v(25.4, 88.9) * mm, "radius": 3.18 * mm});
            skCircle(sketch, "E2.24.11.0", {"center": v(25.4, 63.5) * mm, "radius": 3.18 * mm});
            skCircle(sketch, "E2.24.12.0", {"center": v(25.4, 38.1) * mm, "radius": 3.18 * mm});
            skCircle(sketch, "E2.24.13.0", {"center": v(25.4, 12.7) * mm, "radius": 3.18 * mm});
            skCircle(sketch, "E2.24.14.0", {"center": v(25.4, -12.7) * mm, "radius": 3.18 * mm});
            skCircle(sketch, "E2.24.15.0", {"center": v(25.4, -38.1) * mm, "radius": 3.18 * mm});
            skCircle(sketch, "E2.24.16.0", {"center": v(25.4, -63.5) * mm, "radius": 3.18 * mm});
            skCircle(sketch, "E2.24.17.0", {"center": v(25.4, -88.9) * mm, "radius": 3.18 * mm});
            skCircle(sketch, "E2.24.18.0", {"center": v(25.4, -114.3) * mm, "radius": 3.18 * mm});
            skCircle(sketch, "E2.24.19.0", {"center": v(25.4, -139.7) * mm, "radius": 3.18 * mm});
            skCircle(sketch, "E2.24.20.0", {"center": v(25.4, -165.1) * mm, "radius": 3.18 * mm});
            skCircle(sketch, "E2.24.21.0", {"center": v(25.4, -190.5) * mm, "radius": 3.18 * mm});
            skCircle(sketch, "E2.24.22.0", {"center": v(25.4, -215.9) * mm, "radius": 3.18 * mm});
            skCircle(sketch, "E2.24.23.0", {"center": v(25.4, -241.3) * mm, "radius": 3.18 * mm});
            skCircle(sketch, "E2.24.24.0", {"center": v(25.4, -266.7) * mm, "radius": 3.18 * mm});
            skCircle(sketch, "E2.24.25.0", {"center": v(25.4, -292.1) * mm, "radius": 3.18 * mm});
            skCircle(sketch, "E2.24.26.0", {"center": v(25.4, -317.5) * mm, "radius": 3.18 * mm});
            skCircle(sketch, "E2.24.27.0", {"center": v(25.4, -342.9) * mm, "radius": 3.18 * mm});
            skCircle(sketch, "E2.25.0.0", {"center": v(50.8, 342.9) * mm, "radius": 3.18 * mm});
            skCircle(sketch, "E2.25.1.0", {"center": v(50.8, 317.5) * mm, "radius": 3.18 * mm});
            skCircle(sketch, "E2.25.2.0", {"center": v(50.8, 292.1) * mm, "radius": 3.18 * mm});
            skCircle(sketch, "E2.25.3.0", {"center": v(50.8, 266.7) * mm, "radius": 3.18 * mm});
            skCircle(sketch, "E2.25.4.0", {"center": v(50.8, 241.3) * mm, "radius": 3.18 * mm});
            skCircle(sketch, "E2.25.5.0", {"center": v(50.8, 215.9) * mm, "radius": 3.18 * mm});
            skCircle(sketch, "E2.25.6.0", {"center": v(50.8, 190.5) * mm, "radius": 3.18 * mm});
            skCircle(sketch, "E2.25.7.0", {"center": v(50.8, 165.1) * mm, "radius": 3.18 * mm});
            skCircle(sketch, "E2.25.8.0", {"center": v(50.8, 139.7) * mm, "radius": 3.18 * mm});
            skCircle(sketch, "E2.25.9.0", {"center": v(50.8, 114.3) * mm, "radius": 3.18 * mm});
            skCircle(sketch, "E2.25.10.0", {"center": v(50.8, 88.9) * mm, "radius": 3.18 * mm});
            skCircle(sketch, "E2.25.11.0", {"center": v(50.8, 63.5) * mm, "radius": 3.18 * mm});
            skCircle(sketch, "E2.25.12.0", {"center": v(50.8, 38.1) * mm, "radius": 3.18 * mm});
            skCircle(sketch, "E2.25.13.0", {"center": v(50.8, 12.7) * mm, "radius": 3.18 * mm});
            skCircle(sketch, "E2.25.14.0", {"center": v(50.8, -12.7) * mm, "radius": 3.18 * mm});
            skCircle(sketch, "E2.25.15.0", {"center": v(50.8, -38.1) * mm, "radius": 3.18 * mm});
            skCircle(sketch, "E2.25.16.0", {"center": v(50.8, -63.5) * mm, "radius": 3.18 * mm});
            skCircle(sketch, "E2.25.17.0", {"center": v(50.8, -88.9) * mm, "radius": 3.18 * mm});
            skCircle(sketch, "E2.25.18.0", {"center": v(50.8, -114.3) * mm, "radius": 3.18 * mm});
            skCircle(sketch, "E2.25.19.0", {"center": v(50.8, -139.7) * mm, "radius": 3.18 * mm});
            skCircle(sketch, "E2.25.20.0", {"center": v(50.8, -165.1) * mm, "radius": 3.18 * mm});
            skCircle(sketch, "E2.25.21.0", {"center": v(50.8, -190.5) * mm, "radius": 3.18 * mm});
            skCircle(sketch, "E2.25.22.0", {"center": v(50.8, -215.9) * mm, "radius": 3.18 * mm});
            skCircle(sketch, "E2.25.23.0", {"center": v(50.8, -241.3) * mm, "radius": 3.18 * mm});
            skCircle(sketch, "E2.25.24.0", {"center": v(50.8, -266.7) * mm, "radius": 3.18 * mm});
            skCircle(sketch, "E2.25.25.0", {"center": v(50.8, -292.1) * mm, "radius": 3.18 * mm});
            skCircle(sketch, "E2.25.26.0", {"center": v(50.8, -317.5) * mm, "radius": 3.18 * mm});
            skCircle(sketch, "E2.25.27.0", {"center": v(50.8, -342.9) * mm, "radius": 3.18 * mm});
            skCircle(sketch, "E2.26.0.0", {"center": v(76.2, 342.9) * mm, "radius": 3.18 * mm});
            skCircle(sketch, "E2.26.1.0", {"center": v(76.2, 317.5) * mm, "radius": 3.18 * mm});
            skCircle(sketch, "E2.26.2.0", {"center": v(76.2, 292.1) * mm, "radius": 3.18 * mm});
            skCircle(sketch, "E2.26.3.0", {"center": v(76.2, 266.7) * mm, "radius": 3.18 * mm});
            skCircle(sketch, "E2.26.4.0", {"center": v(76.2, 241.3) * mm, "radius": 3.18 * mm});
            skCircle(sketch, "E2.26.5.0", {"center": v(76.2, 215.9) * mm, "radius": 3.18 * mm});
            skCircle(sketch, "E2.26.6.0", {"center": v(76.2, 190.5) * mm, "radius": 3.18 * mm});
            skCircle(sketch, "E2.26.7.0", {"center": v(76.2, 165.1) * mm, "radius": 3.18 * mm});
            skCircle(sketch, "E2.26.8.0", {"center": v(76.2, 139.7) * mm, "radius": 3.18 * mm});
            skCircle(sketch, "E2.26.9.0", {"center": v(76.2, 114.3) * mm, "radius": 3.18 * mm});
            skCircle(sketch, "E2.26.10.0", {"center": v(76.2, 88.9) * mm, "radius": 3.18 * mm});
            skCircle(sketch, "E2.26.11.0", {"center": v(76.2, 63.5) * mm, "radius": 3.18 * mm});
            skCircle(sketch, "E2.26.12.0", {"center": v(76.2, 38.1) * mm, "radius": 3.18 * mm});
            skCircle(sketch, "E2.26.13.0", {"center": v(76.2, 12.7) * mm, "radius": 3.18 * mm});
            skCircle(sketch, "E2.26.14.0", {"center": v(76.2, -12.7) * mm, "radius": 3.18 * mm});
            skCircle(sketch, "E2.26.15.0", {"center": v(76.2, -38.1) * mm, "radius": 3.18 * mm});
            skCircle(sketch, "E2.26.16.0", {"center": v(76.2, -63.5) * mm, "radius": 3.18 * mm});
            skCircle(sketch, "E2.26.17.0", {"center": v(76.2, -88.9) * mm, "radius": 3.18 * mm});
            skCircle(sketch, "E2.26.18.0", {"center": v(76.2, -114.3) * mm, "radius": 3.18 * mm});
            skCircle(sketch, "E2.26.19.0", {"center": v(76.2, -139.7) * mm, "radius": 3.18 * mm});
            skCircle(sketch, "E2.26.20.0", {"center": v(76.2, -165.1) * mm, "radius": 3.18 * mm});
            skCircle(sketch, "E2.26.21.0", {"center": v(76.2, -190.5) * mm, "radius": 3.18 * mm});
            skCircle(sketch, "E2.26.22.0", {"center": v(76.2, -215.9) * mm, "radius": 3.18 * mm});
            skCircle(sketch, "E2.26.23.0", {"center": v(76.2, -241.3) * mm, "radius": 3.18 * mm});
            skCircle(sketch, "E2.26.24.0", {"center": v(76.2, -266.7) * mm, "radius": 3.18 * mm});
            skCircle(sketch, "E2.26.25.0", {"center": v(76.2, -292.1) * mm, "radius": 3.18 * mm});
            skCircle(sketch, "E2.26.26.0", {"center": v(76.2, -317.5) * mm, "radius": 3.18 * mm});
            skCircle(sketch, "E2.26.27.0", {"center": v(76.2, -342.9) * mm, "radius": 3.18 * mm});
            skCircle(sketch, "E2.27.0.0", {"center": v(101.6, 342.9) * mm, "radius": 3.18 * mm});
            skCircle(sketch, "E2.27.1.0", {"center": v(101.6, 317.5) * mm, "radius": 3.18 * mm});
            skCircle(sketch, "E2.27.2.0", {"center": v(101.6, 292.1) * mm, "radius": 3.18 * mm});
            skCircle(sketch, "E2.27.3.0", {"center": v(101.6, 266.7) * mm, "radius": 3.18 * mm});
            skCircle(sketch, "E2.27.4.0", {"center": v(101.6, 241.3) * mm, "radius": 3.18 * mm});
            skCircle(sketch, "E2.27.5.0", {"center": v(101.6, 215.9) * mm, "radius": 3.18 * mm});
            skCircle(sketch, "E2.27.6.0", {"center": v(101.6, 190.5) * mm, "radius": 3.18 * mm});
            skCircle(sketch, "E2.27.7.0", {"center": v(101.6, 165.1) * mm, "radius": 3.18 * mm});
            skCircle(sketch, "E2.27.8.0", {"center": v(101.6, 139.7) * mm, "radius": 3.18 * mm});
            skCircle(sketch, "E2.27.9.0", {"center": v(101.6, 114.3) * mm, "radius": 3.18 * mm});
            skCircle(sketch, "E2.27.10.0", {"center": v(101.6, 88.9) * mm, "radius": 3.18 * mm});
            skCircle(sketch, "E2.27.11.0", {"center": v(101.6, 63.5) * mm, "radius": 3.18 * mm});
            skCircle(sketch, "E2.27.12.0", {"center": v(101.6, 38.1) * mm, "radius": 3.18 * mm});
            skCircle(sketch, "E2.27.13.0", {"center": v(101.6, 12.7) * mm, "radius": 3.18 * mm});
            skCircle(sketch, "E2.27.14.0", {"center": v(101.6, -12.7) * mm, "radius": 3.18 * mm});
            skCircle(sketch, "E2.27.15.0", {"center": v(101.6, -38.1) * mm, "radius": 3.18 * mm});
            skCircle(sketch, "E2.27.16.0", {"center": v(101.6, -63.5) * mm, "radius": 3.18 * mm});
            skCircle(sketch, "E2.27.17.0", {"center": v(101.6, -88.9) * mm, "radius": 3.18 * mm});
            skCircle(sketch, "E2.27.18.0", {"center": v(101.6, -114.3) * mm, "radius": 3.18 * mm});
            skCircle(sketch, "E2.27.19.0", {"center": v(101.6, -139.7) * mm, "radius": 3.18 * mm});
            skCircle(sketch, "E2.27.20.0", {"center": v(101.6, -165.1) * mm, "radius": 3.18 * mm});
            skCircle(sketch, "E2.27.21.0", {"center": v(101.6, -190.5) * mm, "radius": 3.18 * mm});
            skCircle(sketch, "E2.27.22.0", {"center": v(101.6, -215.9) * mm, "radius": 3.18 * mm});
            skCircle(sketch, "E2.27.23.0", {"center": v(101.6, -241.3) * mm, "radius": 3.18 * mm});
            skCircle(sketch, "E2.27.24.0", {"center": v(101.6, -266.7) * mm, "radius": 3.18 * mm});
            skCircle(sketch, "E2.27.25.0", {"center": v(101.6, -292.1) * mm, "radius": 3.18 * mm});
            skCircle(sketch, "E2.27.26.0", {"center": v(101.6, -317.5) * mm, "radius": 3.18 * mm});
            skCircle(sketch, "E2.27.27.0", {"center": v(101.6, -342.9) * mm, "radius": 3.18 * mm});
            skCircle(sketch, "E2.28.0.0", {"center": v(127, 342.9) * mm, "radius": 3.18 * mm});
            skCircle(sketch, "E2.28.1.0", {"center": v(127, 317.5) * mm, "radius": 3.18 * mm});
            skCircle(sketch, "E2.28.2.0", {"center": v(127, 292.1) * mm, "radius": 3.18 * mm});
            skCircle(sketch, "E2.28.3.0", {"center": v(127, 266.7) * mm, "radius": 3.18 * mm});
            skCircle(sketch, "E2.28.4.0", {"center": v(127, 241.3) * mm, "radius": 3.18 * mm});
            skCircle(sketch, "E2.28.5.0", {"center": v(127, 215.9) * mm, "radius": 3.18 * mm});
            skCircle(sketch, "E2.28.6.0", {"center": v(127, 190.5) * mm, "radius": 3.18 * mm});
            skCircle(sketch, "E2.28.7.0", {"center": v(127, 165.1) * mm, "radius": 3.18 * mm});
            skCircle(sketch, "E2.28.8.0", {"center": v(127, 139.7) * mm, "radius": 3.18 * mm});
            skCircle(sketch, "E2.28.9.0", {"center": v(127, 114.3) * mm, "radius": 3.18 * mm});
            skCircle(sketch, "E2.28.10.0", {"center": v(127, 88.9) * mm, "radius": 3.18 * mm});
            skCircle(sketch, "E2.28.11.0", {"center": v(127, 63.5) * mm, "radius": 3.18 * mm});
            skCircle(sketch, "E2.28.12.0", {"center": v(127, 38.1) * mm, "radius": 3.18 * mm});
            skCircle(sketch, "E2.28.13.0", {"center": v(127, 12.7) * mm, "radius": 3.18 * mm});
            skCircle(sketch, "E2.28.14.0", {"center": v(127, -12.7) * mm, "radius": 3.18 * mm});
            skCircle(sketch, "E2.28.15.0", {"center": v(127, -38.1) * mm, "radius": 3.18 * mm});
            skCircle(sketch, "E2.28.16.0", {"center": v(127, -63.5) * mm, "radius": 3.18 * mm});
            skCircle(sketch, "E2.28.17.0", {"center": v(127, -88.9) * mm, "radius": 3.18 * mm});
            skCircle(sketch, "E2.28.18.0", {"center": v(127, -114.3) * mm, "radius": 3.18 * mm});
            skCircle(sketch, "E2.28.19.0", {"center": v(127, -139.7) * mm, "radius": 3.18 * mm});
            skCircle(sketch, "E2.28.20.0", {"center": v(127, -165.1) * mm, "radius": 3.18 * mm});
            skCircle(sketch, "E2.28.21.0", {"center": v(127, -190.5) * mm, "radius": 3.18 * mm});
            skCircle(sketch, "E2.28.22.0", {"center": v(127, -215.9) * mm, "radius": 3.18 * mm});
            skCircle(sketch, "E2.28.23.0", {"center": v(127, -241.3) * mm, "radius": 3.18 * mm});
            skCircle(sketch, "E2.28.24.0", {"center": v(127, -266.7) * mm, "radius": 3.18 * mm});
            skCircle(sketch, "E2.28.25.0", {"center": v(127, -292.1) * mm, "radius": 3.18 * mm});
            skCircle(sketch, "E2.28.26.0", {"center": v(127, -317.5) * mm, "radius": 3.18 * mm});
            skCircle(sketch, "E2.28.27.0", {"center": v(127, -342.9) * mm, "radius": 3.18 * mm});
            skCircle(sketch, "E2.29.0.0", {"center": v(152.4, 342.9) * mm, "radius": 3.18 * mm});
            skCircle(sketch, "E2.29.1.0", {"center": v(152.4, 317.5) * mm, "radius": 3.18 * mm});
            skCircle(sketch, "E2.29.2.0", {"center": v(152.4, 292.1) * mm, "radius": 3.18 * mm});
            skCircle(sketch, "E2.29.3.0", {"center": v(152.4, 266.7) * mm, "radius": 3.18 * mm});
            skCircle(sketch, "E2.29.4.0", {"center": v(152.4, 241.3) * mm, "radius": 3.18 * mm});
            skCircle(sketch, "E2.29.5.0", {"center": v(152.4, 215.9) * mm, "radius": 3.18 * mm});
            skCircle(sketch, "E2.29.6.0", {"center": v(152.4, 190.5) * mm, "radius": 3.18 * mm});
            skCircle(sketch, "E2.29.7.0", {"center": v(152.4, 165.1) * mm, "radius": 3.18 * mm});
            skCircle(sketch, "E2.29.8.0", {"center": v(152.4, 139.7) * mm, "radius": 3.18 * mm});
            skCircle(sketch, "E2.29.9.0", {"center": v(152.4, 114.3) * mm, "radius": 3.18 * mm});
            skCircle(sketch, "E2.29.10.0", {"center": v(152.4, 88.9) * mm, "radius": 3.18 * mm});
            skCircle(sketch, "E2.29.11.0", {"center": v(152.4, 63.5) * mm, "radius": 3.18 * mm});
            skCircle(sketch, "E2.29.12.0", {"center": v(152.4, 38.1) * mm, "radius": 3.18 * mm});
            skCircle(sketch, "E2.29.13.0", {"center": v(152.4, 12.7) * mm, "radius": 3.18 * mm});
            skCircle(sketch, "E2.29.14.0", {"center": v(152.4, -12.7) * mm, "radius": 3.18 * mm});
            skCircle(sketch, "E2.29.15.0", {"center": v(152.4, -38.1) * mm, "radius": 3.18 * mm});
            skCircle(sketch, "E2.29.16.0", {"center": v(152.4, -63.5) * mm, "radius": 3.18 * mm});
            skCircle(sketch, "E2.29.17.0", {"center": v(152.4, -88.9) * mm, "radius": 3.18 * mm});
            skCircle(sketch, "E2.29.18.0", {"center": v(152.4, -114.3) * mm, "radius": 3.18 * mm});
            skCircle(sketch, "E2.29.19.0", {"center": v(152.4, -139.7) * mm, "radius": 3.18 * mm});
            skCircle(sketch, "E2.29.20.0", {"center": v(152.4, -165.1) * mm, "radius": 3.18 * mm});
            skCircle(sketch, "E2.29.21.0", {"center": v(152.4, -190.5) * mm, "radius": 3.18 * mm});
            skCircle(sketch, "E2.29.22.0", {"center": v(152.4, -215.9) * mm, "radius": 3.18 * mm});
            skCircle(sketch, "E2.29.23.0", {"center": v(152.4, -241.3) * mm, "radius": 3.18 * mm});
            skCircle(sketch, "E2.29.24.0", {"center": v(152.4, -266.7) * mm, "radius": 3.18 * mm});
            skCircle(sketch, "E2.29.25.0", {"center": v(152.4, -292.1) * mm, "radius": 3.18 * mm});
            skCircle(sketch, "E2.29.26.0", {"center": v(152.4, -317.5) * mm, "radius": 3.18 * mm});
            skCircle(sketch, "E2.29.27.0", {"center": v(152.4, -342.9) * mm, "radius": 3.18 * mm});
            skCircle(sketch, "E2.30.0.0", {"center": v(177.8, 342.9) * mm, "radius": 3.18 * mm});
            skCircle(sketch, "E2.30.1.0", {"center": v(177.8, 317.5) * mm, "radius": 3.18 * mm});
            skCircle(sketch, "E2.30.2.0", {"center": v(177.8, 292.1) * mm, "radius": 3.18 * mm});
            skCircle(sketch, "E2.30.3.0", {"center": v(177.8, 266.7) * mm, "radius": 3.18 * mm});
            skCircle(sketch, "E2.30.4.0", {"center": v(177.8, 241.3) * mm, "radius": 3.18 * mm});
            skCircle(sketch, "E2.30.5.0", {"center": v(177.8, 215.9) * mm, "radius": 3.18 * mm});
            skCircle(sketch, "E2.30.6.0", {"center": v(177.8, 190.5) * mm, "radius": 3.18 * mm});
            skCircle(sketch, "E2.30.7.0", {"center": v(177.8, 165.1) * mm, "radius": 3.18 * mm});
            skCircle(sketch, "E2.30.8.0", {"center": v(177.8, 139.7) * mm, "radius": 3.18 * mm});
            skCircle(sketch, "E2.30.9.0", {"center": v(177.8, 114.3) * mm, "radius": 3.18 * mm});
            skCircle(sketch, "E2.30.10.0", {"center": v(177.8, 88.9) * mm, "radius": 3.18 * mm});
            skCircle(sketch, "E2.30.11.0", {"center": v(177.8, 63.5) * mm, "radius": 3.18 * mm});
            skCircle(sketch, "E2.30.12.0", {"center": v(177.8, 38.1) * mm, "radius": 3.18 * mm});
            skCircle(sketch, "E2.30.13.0", {"center": v(177.8, 12.7) * mm, "radius": 3.18 * mm});
            skCircle(sketch, "E2.30.14.0", {"center": v(177.8, -12.7) * mm, "radius": 3.18 * mm});
            skCircle(sketch, "E2.30.15.0", {"center": v(177.8, -38.1) * mm, "radius": 3.18 * mm});
            skCircle(sketch, "E2.30.16.0", {"center": v(177.8, -63.5) * mm, "radius": 3.18 * mm});
            skCircle(sketch, "E2.30.17.0", {"center": v(177.8, -88.9) * mm, "radius": 3.18 * mm});
            skCircle(sketch, "E2.30.18.0", {"center": v(177.8, -114.3) * mm, "radius": 3.18 * mm});
            skCircle(sketch, "E2.30.19.0", {"center": v(177.8, -139.7) * mm, "radius": 3.18 * mm});
            skCircle(sketch, "E2.30.20.0", {"center": v(177.8, -165.1) * mm, "radius": 3.18 * mm});
            skCircle(sketch, "E2.30.21.0", {"center": v(177.8, -190.5) * mm, "radius": 3.18 * mm});
            skCircle(sketch, "E2.30.22.0", {"center": v(177.8, -215.9) * mm, "radius": 3.18 * mm});
            skCircle(sketch, "E2.30.23.0", {"center": v(177.8, -241.3) * mm, "radius": 3.18 * mm});
            skCircle(sketch, "E2.30.24.0", {"center": v(177.8, -266.7) * mm, "radius": 3.18 * mm});
            skCircle(sketch, "E2.30.25.0", {"center": v(177.8, -292.1) * mm, "radius": 3.18 * mm});
            skCircle(sketch, "E2.30.26.0", {"center": v(177.8, -317.5) * mm, "radius": 3.18 * mm});
            skCircle(sketch, "E2.30.27.0", {"center": v(177.8, -342.9) * mm, "radius": 3.18 * mm});
            skCircle(sketch, "E2.31.0.0", {"center": v(203.2, 342.9) * mm, "radius": 3.18 * mm});
            skCircle(sketch, "E2.31.1.0", {"center": v(203.2, 317.5) * mm, "radius": 3.18 * mm});
            skCircle(sketch, "E2.31.2.0", {"center": v(203.2, 292.1) * mm, "radius": 3.18 * mm});
            skCircle(sketch, "E2.31.3.0", {"center": v(203.2, 266.7) * mm, "radius": 3.18 * mm});
            skCircle(sketch, "E2.31.4.0", {"center": v(203.2, 241.3) * mm, "radius": 3.18 * mm});
            skCircle(sketch, "E2.31.5.0", {"center": v(203.2, 215.9) * mm, "radius": 3.18 * mm});
            skCircle(sketch, "E2.31.6.0", {"center": v(203.2, 190.5) * mm, "radius": 3.18 * mm});
            skCircle(sketch, "E2.31.7.0", {"center": v(203.2, 165.1) * mm, "radius": 3.18 * mm});
            skCircle(sketch, "E2.31.8.0", {"center": v(203.2, 139.7) * mm, "radius": 3.18 * mm});
            skCircle(sketch, "E2.31.9.0", {"center": v(203.2, 114.3) * mm, "radius": 3.18 * mm});
            skCircle(sketch, "E2.31.10.0", {"center": v(203.2, 88.9) * mm, "radius": 3.18 * mm});
            skCircle(sketch, "E2.31.11.0", {"center": v(203.2, 63.5) * mm, "radius": 3.18 * mm});
            skCircle(sketch, "E2.31.12.0", {"center": v(203.2, 38.1) * mm, "radius": 3.18 * mm});
            skCircle(sketch, "E2.31.13.0", {"center": v(203.2, 12.7) * mm, "radius": 3.18 * mm});
            skCircle(sketch, "E2.31.14.0", {"center": v(203.2, -12.7) * mm, "radius": 3.18 * mm});
            skCircle(sketch, "E2.31.15.0", {"center": v(203.2, -38.1) * mm, "radius": 3.18 * mm});
            skCircle(sketch, "E2.31.16.0", {"center": v(203.2, -63.5) * mm, "radius": 3.18 * mm});
            skCircle(sketch, "E2.31.17.0", {"center": v(203.2, -88.9) * mm, "radius": 3.18 * mm});
            skCircle(sketch, "E2.31.18.0", {"center": v(203.2, -114.3) * mm, "radius": 3.18 * mm});
            skCircle(sketch, "E2.31.19.0", {"center": v(203.2, -139.7) * mm, "radius": 3.18 * mm});
            skCircle(sketch, "E2.31.20.0", {"center": v(203.2, -165.1) * mm, "radius": 3.18 * mm});
            skCircle(sketch, "E2.31.21.0", {"center": v(203.2, -190.5) * mm, "radius": 3.18 * mm});
            skCircle(sketch, "E2.31.22.0", {"center": v(203.2, -215.9) * mm, "radius": 3.18 * mm});
            skCircle(sketch, "E2.31.23.0", {"center": v(203.2, -241.3) * mm, "radius": 3.18 * mm});
            skCircle(sketch, "E2.31.24.0", {"center": v(203.2, -266.7) * mm, "radius": 3.18 * mm});
            skCircle(sketch, "E2.31.25.0", {"center": v(203.2, -292.1) * mm, "radius": 3.18 * mm});
            skCircle(sketch, "E2.31.26.0", {"center": v(203.2, -317.5) * mm, "radius": 3.18 * mm});
            skCircle(sketch, "E2.31.27.0", {"center": v(203.2, -342.9) * mm, "radius": 3.18 * mm});
            skCircle(sketch, "E2.32.0.0", {"center": v(228.6, 342.9) * mm, "radius": 3.18 * mm});
            skCircle(sketch, "E2.32.1.0", {"center": v(228.6, 317.5) * mm, "radius": 3.18 * mm});
            skCircle(sketch, "E2.32.2.0", {"center": v(228.6, 292.1) * mm, "radius": 3.18 * mm});
            skCircle(sketch, "E2.32.3.0", {"center": v(228.6, 266.7) * mm, "radius": 3.18 * mm});
            skCircle(sketch, "E2.32.4.0", {"center": v(228.6, 241.3) * mm, "radius": 3.18 * mm});
            skCircle(sketch, "E2.32.5.0", {"center": v(228.6, 215.9) * mm, "radius": 3.18 * mm});
            skCircle(sketch, "E2.32.6.0", {"center": v(228.6, 190.5) * mm, "radius": 3.18 * mm});
            skCircle(sketch, "E2.32.7.0", {"center": v(228.6, 165.1) * mm, "radius": 3.18 * mm});
            skCircle(sketch, "E2.32.8.0", {"center": v(228.6, 139.7) * mm, "radius": 3.18 * mm});
            skCircle(sketch, "E2.32.9.0", {"center": v(228.6, 114.3) * mm, "radius": 3.18 * mm});
            skCircle(sketch, "E2.32.10.0", {"center": v(228.6, 88.9) * mm, "radius": 3.18 * mm});
            skCircle(sketch, "E2.32.11.0", {"center": v(228.6, 63.5) * mm, "radius": 3.18 * mm});
            skCircle(sketch, "E2.32.12.0", {"center": v(228.6, 38.1) * mm, "radius": 3.18 * mm});
            skCircle(sketch, "E2.32.13.0", {"center": v(228.6, 12.7) * mm, "radius": 3.18 * mm});
            skCircle(sketch, "E2.32.14.0", {"center": v(228.6, -12.7) * mm, "radius": 3.18 * mm});
            skCircle(sketch, "E2.32.15.0", {"center": v(228.6, -38.1) * mm, "radius": 3.18 * mm});
            skCircle(sketch, "E2.32.16.0", {"center": v(228.6, -63.5) * mm, "radius": 3.18 * mm});
            skCircle(sketch, "E2.32.17.0", {"center": v(228.6, -88.9) * mm, "radius": 3.18 * mm});
            skCircle(sketch, "E2.32.18.0", {"center": v(228.6, -114.3) * mm, "radius": 3.18 * mm});
            skCircle(sketch, "E2.32.19.0", {"center": v(228.6, -139.7) * mm, "radius": 3.18 * mm});
            skCircle(sketch, "E2.32.20.0", {"center": v(228.6, -165.1) * mm, "radius": 3.18 * mm});
            skCircle(sketch, "E2.32.21.0", {"center": v(228.6, -190.5) * mm, "radius": 3.18 * mm});
            skCircle(sketch, "E2.32.22.0", {"center": v(228.6, -215.9) * mm, "radius": 3.18 * mm});
            skCircle(sketch, "E2.32.23.0", {"center": v(228.6, -241.3) * mm, "radius": 3.18 * mm});
            skCircle(sketch, "E2.32.24.0", {"center": v(228.6, -266.7) * mm, "radius": 3.18 * mm});
            skCircle(sketch, "E2.32.25.0", {"center": v(228.6, -292.1) * mm, "radius": 3.18 * mm});
            skCircle(sketch, "E2.32.26.0", {"center": v(228.6, -317.5) * mm, "radius": 3.18 * mm});
            skCircle(sketch, "E2.32.27.0", {"center": v(228.6, -342.9) * mm, "radius": 3.18 * mm});
            skCircle(sketch, "E2.33.0.0", {"center": v(254, 342.9) * mm, "radius": 3.18 * mm});
            skCircle(sketch, "E2.33.1.0", {"center": v(254, 317.5) * mm, "radius": 3.18 * mm});
            skCircle(sketch, "E2.33.2.0", {"center": v(254, 292.1) * mm, "radius": 3.18 * mm});
            skCircle(sketch, "E2.33.3.0", {"center": v(254, 266.7) * mm, "radius": 3.18 * mm});
            skCircle(sketch, "E2.33.4.0", {"center": v(254, 241.3) * mm, "radius": 3.18 * mm});
            skCircle(sketch, "E2.33.5.0", {"center": v(254, 215.9) * mm, "radius": 3.18 * mm});
            skCircle(sketch, "E2.33.6.0", {"center": v(254, 190.5) * mm, "radius": 3.18 * mm});
            skCircle(sketch, "E2.33.7.0", {"center": v(254, 165.1) * mm, "radius": 3.18 * mm});
            skCircle(sketch, "E2.33.8.0", {"center": v(254, 139.7) * mm, "radius": 3.18 * mm});
            skCircle(sketch, "E2.33.9.0", {"center": v(254, 114.3) * mm, "radius": 3.18 * mm});
            skCircle(sketch, "E2.33.10.0", {"center": v(254, 88.9) * mm, "radius": 3.18 * mm});
            skCircle(sketch, "E2.33.11.0", {"center": v(254, 63.5) * mm, "radius": 3.18 * mm});
            skCircle(sketch, "E2.33.12.0", {"center": v(254, 38.1) * mm, "radius": 3.18 * mm});
            skCircle(sketch, "E2.33.13.0", {"center": v(254, 12.7) * mm, "radius": 3.18 * mm});
            skCircle(sketch, "E2.33.14.0", {"center": v(254, -12.7) * mm, "radius": 3.18 * mm});
            skCircle(sketch, "E2.33.15.0", {"center": v(254, -38.1) * mm, "radius": 3.18 * mm});
            skCircle(sketch, "E2.33.16.0", {"center": v(254, -63.5) * mm, "radius": 3.18 * mm});
            skCircle(sketch, "E2.33.17.0", {"center": v(254, -88.9) * mm, "radius": 3.18 * mm});
            skCircle(sketch, "E2.33.18.0", {"center": v(254, -114.3) * mm, "radius": 3.18 * mm});
            skCircle(sketch, "E2.33.19.0", {"center": v(254, -139.7) * mm, "radius": 3.18 * mm});
            skCircle(sketch, "E2.33.20.0", {"center": v(254, -165.1) * mm, "radius": 3.18 * mm});
            skCircle(sketch, "E2.33.21.0", {"center": v(254, -190.5) * mm, "radius": 3.18 * mm});
            skCircle(sketch, "E2.33.22.0", {"center": v(254, -215.9) * mm, "radius": 3.18 * mm});
            skCircle(sketch, "E2.33.23.0", {"center": v(254, -241.3) * mm, "radius": 3.18 * mm});
            skCircle(sketch, "E2.33.24.0", {"center": v(254, -266.7) * mm, "radius": 3.18 * mm});
            skCircle(sketch, "E2.33.25.0", {"center": v(254, -292.1) * mm, "radius": 3.18 * mm});
            skCircle(sketch, "E2.33.26.0", {"center": v(254, -317.5) * mm, "radius": 3.18 * mm});
            skCircle(sketch, "E2.33.27.0", {"center": v(254, -342.9) * mm, "radius": 3.18 * mm});
            skCircle(sketch, "E2.34.0.0", {"center": v(279.4, 342.9) * mm, "radius": 3.18 * mm});
            skCircle(sketch, "E2.34.1.0", {"center": v(279.4, 317.5) * mm, "radius": 3.18 * mm});
            skCircle(sketch, "E2.34.2.0", {"center": v(279.4, 292.1) * mm, "radius": 3.18 * mm});
            skCircle(sketch, "E2.34.3.0", {"center": v(279.4, 266.7) * mm, "radius": 3.18 * mm});
            skCircle(sketch, "E2.34.4.0", {"center": v(279.4, 241.3) * mm, "radius": 3.18 * mm});
            skCircle(sketch, "E2.34.5.0", {"center": v(279.4, 215.9) * mm, "radius": 3.18 * mm});
            skCircle(sketch, "E2.34.6.0", {"center": v(279.4, 190.5) * mm, "radius": 3.18 * mm});
            skCircle(sketch, "E2.34.7.0", {"center": v(279.4, 165.1) * mm, "radius": 3.18 * mm});
            skCircle(sketch, "E2.34.8.0", {"center": v(279.4, 139.7) * mm, "radius": 3.18 * mm});
            skCircle(sketch, "E2.34.9.0", {"center": v(279.4, 114.3) * mm, "radius": 3.18 * mm});
            skCircle(sketch, "E2.34.10.0", {"center": v(279.4, 88.9) * mm, "radius": 3.18 * mm});
            skCircle(sketch, "E2.34.11.0", {"center": v(279.4, 63.5) * mm, "radius": 3.18 * mm});
            skCircle(sketch, "E2.34.12.0", {"center": v(279.4, 38.1) * mm, "radius": 3.18 * mm});
            skCircle(sketch, "E2.34.13.0", {"center": v(279.4, 12.7) * mm, "radius": 3.18 * mm});
            skCircle(sketch, "E2.34.14.0", {"center": v(279.4, -12.7) * mm, "radius": 3.18 * mm});
            skCircle(sketch, "E2.34.15.0", {"center": v(279.4, -38.1) * mm, "radius": 3.18 * mm});
            skCircle(sketch, "E2.34.16.0", {"center": v(279.4, -63.5) * mm, "radius": 3.18 * mm});
            skCircle(sketch, "E2.34.17.0", {"center": v(279.4, -88.9) * mm, "radius": 3.18 * mm});
            skCircle(sketch, "E2.34.18.0", {"center": v(279.4, -114.3) * mm, "radius": 3.18 * mm});
            skCircle(sketch, "E2.34.19.0", {"center": v(279.4, -139.7) * mm, "radius": 3.18 * mm});
            skCircle(sketch, "E2.34.20.0", {"center": v(279.4, -165.1) * mm, "radius": 3.18 * mm});
            skCircle(sketch, "E2.34.21.0", {"center": v(279.4, -190.5) * mm, "radius": 3.18 * mm});
            skCircle(sketch, "E2.34.22.0", {"center": v(279.4, -215.9) * mm, "radius": 3.18 * mm});
            skCircle(sketch, "E2.34.23.0", {"center": v(279.4, -241.3) * mm, "radius": 3.18 * mm});
            skCircle(sketch, "E2.34.24.0", {"center": v(279.4, -266.7) * mm, "radius": 3.18 * mm});
            skCircle(sketch, "E2.34.25.0", {"center": v(279.4, -292.1) * mm, "radius": 3.18 * mm});
            skCircle(sketch, "E2.34.26.0", {"center": v(279.4, -317.5) * mm, "radius": 3.18 * mm});
            skCircle(sketch, "E2.34.27.0", {"center": v(279.4, -342.9) * mm, "radius": 3.18 * mm});
            skCircle(sketch, "E2.35.0.0", {"center": v(304.8, 342.9) * mm, "radius": 3.18 * mm});
            skCircle(sketch, "E2.35.1.0", {"center": v(304.8, 317.5) * mm, "radius": 3.18 * mm});
            skCircle(sketch, "E2.35.2.0", {"center": v(304.8, 292.1) * mm, "radius": 3.18 * mm});
            skCircle(sketch, "E2.35.3.0", {"center": v(304.8, 266.7) * mm, "radius": 3.18 * mm});
            skCircle(sketch, "E2.35.4.0", {"center": v(304.8, 241.3) * mm, "radius": 3.18 * mm});
            skCircle(sketch, "E2.35.5.0", {"center": v(304.8, 215.9) * mm, "radius": 3.18 * mm});
            skCircle(sketch, "E2.35.6.0", {"center": v(304.8, 190.5) * mm, "radius": 3.18 * mm});
            skCircle(sketch, "E2.35.7.0", {"center": v(304.8, 165.1) * mm, "radius": 3.18 * mm});
            skCircle(sketch, "E2.35.8.0", {"center": v(304.8, 139.7) * mm, "radius": 3.18 * mm});
            skCircle(sketch, "E2.35.9.0", {"center": v(304.8, 114.3) * mm, "radius": 3.18 * mm});
            skCircle(sketch, "E2.35.10.0", {"center": v(304.8, 88.9) * mm, "radius": 3.18 * mm});
            skCircle(sketch, "E2.35.11.0", {"center": v(304.8, 63.5) * mm, "radius": 3.18 * mm});
            skCircle(sketch, "E2.35.12.0", {"center": v(304.8, 38.1) * mm, "radius": 3.18 * mm});
            skCircle(sketch, "E2.35.13.0", {"center": v(304.8, 12.7) * mm, "radius": 3.18 * mm});
            skCircle(sketch, "E2.35.14.0", {"center": v(304.8, -12.7) * mm, "radius": 3.18 * mm});
            skCircle(sketch, "E2.35.15.0", {"center": v(304.8, -38.1) * mm, "radius": 3.18 * mm});
            skCircle(sketch, "E2.35.16.0", {"center": v(304.8, -63.5) * mm, "radius": 3.18 * mm});
            skCircle(sketch, "E2.35.17.0", {"center": v(304.8, -88.9) * mm, "radius": 3.18 * mm});
            skCircle(sketch, "E2.35.18.0", {"center": v(304.8, -114.3) * mm, "radius": 3.18 * mm});
            skCircle(sketch, "E2.35.19.0", {"center": v(304.8, -139.7) * mm, "radius": 3.18 * mm});
            skCircle(sketch, "E2.35.20.0", {"center": v(304.8, -165.1) * mm, "radius": 3.18 * mm});
            skCircle(sketch, "E2.35.21.0", {"center": v(304.8, -190.5) * mm, "radius": 3.18 * mm});
            skCircle(sketch, "E2.35.22.0", {"center": v(304.8, -215.9) * mm, "radius": 3.18 * mm});
            skCircle(sketch, "E2.35.23.0", {"center": v(304.8, -241.3) * mm, "radius": 3.18 * mm});
            skCircle(sketch, "E2.35.24.0", {"center": v(304.8, -266.7) * mm, "radius": 3.18 * mm});
            skCircle(sketch, "E2.35.25.0", {"center": v(304.8, -292.1) * mm, "radius": 3.18 * mm});
            skCircle(sketch, "E2.35.26.0", {"center": v(304.8, -317.5) * mm, "radius": 3.18 * mm});
            skCircle(sketch, "E2.35.27.0", {"center": v(304.8, -342.9) * mm, "radius": 3.18 * mm});
            skCircle(sketch, "E2.36.0.0", {"center": v(330.2, 342.9) * mm, "radius": 3.18 * mm});
            skCircle(sketch, "E2.36.1.0", {"center": v(330.2, 317.5) * mm, "radius": 3.18 * mm});
            skCircle(sketch, "E2.36.2.0", {"center": v(330.2, 292.1) * mm, "radius": 3.18 * mm});
            skCircle(sketch, "E2.36.3.0", {"center": v(330.2, 266.7) * mm, "radius": 3.18 * mm});
            skCircle(sketch, "E2.36.4.0", {"center": v(330.2, 241.3) * mm, "radius": 3.18 * mm});
            skCircle(sketch, "E2.36.5.0", {"center": v(330.2, 215.9) * mm, "radius": 3.18 * mm});
            skCircle(sketch, "E2.36.6.0", {"center": v(330.2, 190.5) * mm, "radius": 3.18 * mm});
            skCircle(sketch, "E2.36.7.0", {"center": v(330.2, 165.1) * mm, "radius": 3.18 * mm});
            skCircle(sketch, "E2.36.8.0", {"center": v(330.2, 139.7) * mm, "radius": 3.18 * mm});
            skCircle(sketch, "E2.36.9.0", {"center": v(330.2, 114.3) * mm, "radius": 3.18 * mm});
            skCircle(sketch, "E2.36.10.0", {"center": v(330.2, 88.9) * mm, "radius": 3.18 * mm});
            skCircle(sketch, "E2.36.11.0", {"center": v(330.2, 63.5) * mm, "radius": 3.18 * mm});
            skCircle(sketch, "E2.36.12.0", {"center": v(330.2, 38.1) * mm, "radius": 3.18 * mm});
            skCircle(sketch, "E2.36.13.0", {"center": v(330.2, 12.7) * mm, "radius": 3.18 * mm});
            skCircle(sketch, "E2.36.14.0", {"center": v(330.2, -12.7) * mm, "radius": 3.18 * mm});
            skCircle(sketch, "E2.36.15.0", {"center": v(330.2, -38.1) * mm, "radius": 3.18 * mm});
            skCircle(sketch, "E2.36.16.0", {"center": v(330.2, -63.5) * mm, "radius": 3.18 * mm});
            skCircle(sketch, "E2.36.17.0", {"center": v(330.2, -88.9) * mm, "radius": 3.18 * mm});
            skCircle(sketch, "E2.36.18.0", {"center": v(330.2, -114.3) * mm, "radius": 3.18 * mm});
            skCircle(sketch, "E2.36.19.0", {"center": v(330.2, -139.7) * mm, "radius": 3.18 * mm});
            skCircle(sketch, "E2.36.20.0", {"center": v(330.2, -165.1) * mm, "radius": 3.18 * mm});
            skCircle(sketch, "E2.36.21.0", {"center": v(330.2, -190.5) * mm, "radius": 3.18 * mm});
            skCircle(sketch, "E2.36.22.0", {"center": v(330.2, -215.9) * mm, "radius": 3.18 * mm});
            skCircle(sketch, "E2.36.23.0", {"center": v(330.2, -241.3) * mm, "radius": 3.18 * mm});
            skCircle(sketch, "E2.36.24.0", {"center": v(330.2, -266.7) * mm, "radius": 3.18 * mm});
            skCircle(sketch, "E2.36.25.0", {"center": v(330.2, -292.1) * mm, "radius": 3.18 * mm});
            skCircle(sketch, "E2.36.26.0", {"center": v(330.2, -317.5) * mm, "radius": 3.18 * mm});
            skCircle(sketch, "E2.36.27.0", {"center": v(330.2, -342.9) * mm, "radius": 3.18 * mm});
            skCircle(sketch, "E2.37.0.0", {"center": v(355.6, 342.9) * mm, "radius": 3.18 * mm});
            skCircle(sketch, "E2.37.1.0", {"center": v(355.6, 317.5) * mm, "radius": 3.18 * mm});
            skCircle(sketch, "E2.37.2.0", {"center": v(355.6, 292.1) * mm, "radius": 3.18 * mm});
            skCircle(sketch, "E2.37.3.0", {"center": v(355.6, 266.7) * mm, "radius": 3.18 * mm});
            skCircle(sketch, "E2.37.4.0", {"center": v(355.6, 241.3) * mm, "radius": 3.18 * mm});
            skCircle(sketch, "E2.37.5.0", {"center": v(355.6, 215.9) * mm, "radius": 3.18 * mm});
            skCircle(sketch, "E2.37.6.0", {"center": v(355.6, 190.5) * mm, "radius": 3.18 * mm});
            skCircle(sketch, "E2.37.7.0", {"center": v(355.6, 165.1) * mm, "radius": 3.18 * mm});
            skCircle(sketch, "E2.37.8.0", {"center": v(355.6, 139.7) * mm, "radius": 3.18 * mm});
            skCircle(sketch, "E2.37.9.0", {"center": v(355.6, 114.3) * mm, "radius": 3.18 * mm});
            skCircle(sketch, "E2.37.10.0", {"center": v(355.6, 88.9) * mm, "radius": 3.18 * mm});
            skCircle(sketch, "E2.37.11.0", {"center": v(355.6, 63.5) * mm, "radius": 3.18 * mm});
            skCircle(sketch, "E2.37.12.0", {"center": v(355.6, 38.1) * mm, "radius": 3.18 * mm});
            skCircle(sketch, "E2.37.13.0", {"center": v(355.6, 12.7) * mm, "radius": 3.18 * mm});
            skCircle(sketch, "E2.37.14.0", {"center": v(355.6, -12.7) * mm, "radius": 3.18 * mm});
            skCircle(sketch, "E2.37.15.0", {"center": v(355.6, -38.1) * mm, "radius": 3.18 * mm});
            skCircle(sketch, "E2.37.16.0", {"center": v(355.6, -63.5) * mm, "radius": 3.18 * mm});
            skCircle(sketch, "E2.37.17.0", {"center": v(355.6, -88.9) * mm, "radius": 3.18 * mm});
            skCircle(sketch, "E2.37.18.0", {"center": v(355.6, -114.3) * mm, "radius": 3.18 * mm});
            skCircle(sketch, "E2.37.19.0", {"center": v(355.6, -139.7) * mm, "radius": 3.18 * mm});
            skCircle(sketch, "E2.37.20.0", {"center": v(355.6, -165.1) * mm, "radius": 3.18 * mm});
            skCircle(sketch, "E2.37.21.0", {"center": v(355.6, -190.5) * mm, "radius": 3.18 * mm});
            skCircle(sketch, "E2.37.22.0", {"center": v(355.6, -215.9) * mm, "radius": 3.18 * mm});
            skCircle(sketch, "E2.37.23.0", {"center": v(355.6, -241.3) * mm, "radius": 3.18 * mm});
            skCircle(sketch, "E2.37.24.0", {"center": v(355.6, -266.7) * mm, "radius": 3.18 * mm});
            skCircle(sketch, "E2.37.25.0", {"center": v(355.6, -292.1) * mm, "radius": 3.18 * mm});
            skCircle(sketch, "E2.37.26.0", {"center": v(355.6, -317.5) * mm, "radius": 3.18 * mm});
            skCircle(sketch, "E2.37.27.0", {"center": v(355.6, -342.9) * mm, "radius": 3.18 * mm});
            skCircle(sketch, "E2.38.0.0", {"center": v(381, 342.9) * mm, "radius": 3.18 * mm});
            skCircle(sketch, "E2.38.1.0", {"center": v(381, 317.5) * mm, "radius": 3.18 * mm});
            skCircle(sketch, "E2.38.2.0", {"center": v(381, 292.1) * mm, "radius": 3.18 * mm});
            skCircle(sketch, "E2.38.3.0", {"center": v(381, 266.7) * mm, "radius": 3.18 * mm});
            skCircle(sketch, "E2.38.4.0", {"center": v(381, 241.3) * mm, "radius": 3.18 * mm});
            skCircle(sketch, "E2.38.5.0", {"center": v(381, 215.9) * mm, "radius": 3.18 * mm});
            skCircle(sketch, "E2.38.6.0", {"center": v(381, 190.5) * mm, "radius": 3.18 * mm});
            skCircle(sketch, "E2.38.7.0", {"center": v(381, 165.1) * mm, "radius": 3.18 * mm});
            skCircle(sketch, "E2.38.8.0", {"center": v(381, 139.7) * mm, "radius": 3.18 * mm});
            skCircle(sketch, "E2.38.9.0", {"center": v(381, 114.3) * mm, "radius": 3.18 * mm});
            skCircle(sketch, "E2.38.10.0", {"center": v(381, 88.9) * mm, "radius": 3.18 * mm});
            skCircle(sketch, "E2.38.11.0", {"center": v(381, 63.5) * mm, "radius": 3.18 * mm});
            skCircle(sketch, "E2.38.12.0", {"center": v(381, 38.1) * mm, "radius": 3.18 * mm});
            skCircle(sketch, "E2.38.13.0", {"center": v(381, 12.7) * mm, "radius": 3.18 * mm});
            skCircle(sketch, "E2.38.14.0", {"center": v(381, -12.7) * mm, "radius": 3.18 * mm});
            skCircle(sketch, "E2.38.15.0", {"center": v(381, -38.1) * mm, "radius": 3.18 * mm});
            skCircle(sketch, "E2.38.16.0", {"center": v(381, -63.5) * mm, "radius": 3.18 * mm});
            skCircle(sketch, "E2.38.17.0", {"center": v(381, -88.9) * mm, "radius": 3.18 * mm});
            skCircle(sketch, "E2.38.18.0", {"center": v(381, -114.3) * mm, "radius": 3.18 * mm});
            skCircle(sketch, "E2.38.19.0", {"center": v(381, -139.7) * mm, "radius": 3.18 * mm});
            skCircle(sketch, "E2.38.20.0", {"center": v(381, -165.1) * mm, "radius": 3.18 * mm});
            skCircle(sketch, "E2.38.21.0", {"center": v(381, -190.5) * mm, "radius": 3.18 * mm});
            skCircle(sketch, "E2.38.22.0", {"center": v(381, -215.9) * mm, "radius": 3.18 * mm});
            skCircle(sketch, "E2.38.23.0", {"center": v(381, -241.3) * mm, "radius": 3.18 * mm});
            skCircle(sketch, "E2.38.24.0", {"center": v(381, -266.7) * mm, "radius": 3.18 * mm});
            skCircle(sketch, "E2.38.25.0", {"center": v(381, -292.1) * mm, "radius": 3.18 * mm});
            skCircle(sketch, "E2.38.26.0", {"center": v(381, -317.5) * mm, "radius": 3.18 * mm});
            skCircle(sketch, "E2.38.27.0", {"center": v(381, -342.9) * mm, "radius": 3.18 * mm});
            skCircle(sketch, "E2.39.0.0", {"center": v(406.4, 342.9) * mm, "radius": 3.18 * mm});
            skCircle(sketch, "E2.39.1.0", {"center": v(406.4, 317.5) * mm, "radius": 3.18 * mm});
            skCircle(sketch, "E2.39.2.0", {"center": v(406.4, 292.1) * mm, "radius": 3.18 * mm});
            skCircle(sketch, "E2.39.3.0", {"center": v(406.4, 266.7) * mm, "radius": 3.18 * mm});
            skCircle(sketch, "E2.39.4.0", {"center": v(406.4, 241.3) * mm, "radius": 3.18 * mm});
            skCircle(sketch, "E2.39.5.0", {"center": v(406.4, 215.9) * mm, "radius": 3.18 * mm});
            skCircle(sketch, "E2.39.6.0", {"center": v(406.4, 190.5) * mm, "radius": 3.18 * mm});
            skCircle(sketch, "E2.39.7.0", {"center": v(406.4, 165.1) * mm, "radius": 3.18 * mm});
            skCircle(sketch, "E2.39.8.0", {"center": v(406.4, 139.7) * mm, "radius": 3.18 * mm});
            skCircle(sketch, "E2.39.9.0", {"center": v(406.4, 114.3) * mm, "radius": 3.18 * mm});
            skCircle(sketch, "E2.39.10.0", {"center": v(406.4, 88.9) * mm, "radius": 3.18 * mm});
            skCircle(sketch, "E2.39.11.0", {"center": v(406.4, 63.5) * mm, "radius": 3.18 * mm});
            skCircle(sketch, "E2.39.12.0", {"center": v(406.4, 38.1) * mm, "radius": 3.18 * mm});
            skCircle(sketch, "E2.39.13.0", {"center": v(406.4, 12.7) * mm, "radius": 3.18 * mm});
            skCircle(sketch, "E2.39.14.0", {"center": v(406.4, -12.7) * mm, "radius": 3.18 * mm});
            skCircle(sketch, "E2.39.15.0", {"center": v(406.4, -38.1) * mm, "radius": 3.18 * mm});
            skCircle(sketch, "E2.39.16.0", {"center": v(406.4, -63.5) * mm, "radius": 3.18 * mm});
            skCircle(sketch, "E2.39.17.0", {"center": v(406.4, -88.9) * mm, "radius": 3.18 * mm});
            skCircle(sketch, "E2.39.18.0", {"center": v(406.4, -114.3) * mm, "radius": 3.18 * mm});
            skCircle(sketch, "E2.39.19.0", {"center": v(406.4, -139.7) * mm, "radius": 3.18 * mm});
            skCircle(sketch, "E2.39.20.0", {"center": v(406.4, -165.1) * mm, "radius": 3.18 * mm});
            skCircle(sketch, "E2.39.21.0", {"center": v(406.4, -190.5) * mm, "radius": 3.18 * mm});
            skCircle(sketch, "E2.39.22.0", {"center": v(406.4, -215.9) * mm, "radius": 3.18 * mm});
            skCircle(sketch, "E2.39.23.0", {"center": v(406.4, -241.3) * mm, "radius": 3.18 * mm});
            skCircle(sketch, "E2.39.24.0", {"center": v(406.4, -266.7) * mm, "radius": 3.18 * mm});
            skCircle(sketch, "E2.39.25.0", {"center": v(406.4, -292.1) * mm, "radius": 3.18 * mm});
            skCircle(sketch, "E2.39.26.0", {"center": v(406.4, -317.5) * mm, "radius": 3.18 * mm});
            skCircle(sketch, "E2.39.27.0", {"center": v(406.4, -342.9) * mm, "radius": 3.18 * mm});
            skCircle(sketch, "E2.40.0.0", {"center": v(431.8, 342.9) * mm, "radius": 3.18 * mm});
            skCircle(sketch, "E2.40.1.0", {"center": v(431.8, 317.5) * mm, "radius": 3.18 * mm});
            skCircle(sketch, "E2.40.2.0", {"center": v(431.8, 292.1) * mm, "radius": 3.18 * mm});
            skCircle(sketch, "E2.40.3.0", {"center": v(431.8, 266.7) * mm, "radius": 3.18 * mm});
            skCircle(sketch, "E2.40.4.0", {"center": v(431.8, 241.3) * mm, "radius": 3.18 * mm});
            skCircle(sketch, "E2.40.5.0", {"center": v(431.8, 215.9) * mm, "radius": 3.18 * mm});
            skCircle(sketch, "E2.40.6.0", {"center": v(431.8, 190.5) * mm, "radius": 3.18 * mm});
            skCircle(sketch, "E2.40.7.0", {"center": v(431.8, 165.1) * mm, "radius": 3.18 * mm});
            skCircle(sketch, "E2.40.8.0", {"center": v(431.8, 139.7) * mm, "radius": 3.18 * mm});
            skCircle(sketch, "E2.40.9.0", {"center": v(431.8, 114.3) * mm, "radius": 3.18 * mm});
            skCircle(sketch, "E2.40.10.0", {"center": v(431.8, 88.9) * mm, "radius": 3.18 * mm});
            skCircle(sketch, "E2.40.11.0", {"center": v(431.8, 63.5) * mm, "radius": 3.18 * mm});
            skCircle(sketch, "E2.40.12.0", {"center": v(431.8, 38.1) * mm, "radius": 3.18 * mm});
            skCircle(sketch, "E2.40.13.0", {"center": v(431.8, 12.7) * mm, "radius": 3.18 * mm});
            skCircle(sketch, "E2.40.14.0", {"center": v(431.8, -12.7) * mm, "radius": 3.18 * mm});
            skCircle(sketch, "E2.40.15.0", {"center": v(431.8, -38.1) * mm, "radius": 3.18 * mm});
            skCircle(sketch, "E2.40.16.0", {"center": v(431.8, -63.5) * mm, "radius": 3.18 * mm});
            skCircle(sketch, "E2.40.17.0", {"center": v(431.8, -88.9) * mm, "radius": 3.18 * mm});
            skCircle(sketch, "E2.40.18.0", {"center": v(431.8, -114.3) * mm, "radius": 3.18 * mm});
            skCircle(sketch, "E2.40.19.0", {"center": v(431.8, -139.7) * mm, "radius": 3.18 * mm});
            skCircle(sketch, "E2.40.20.0", {"center": v(431.8, -165.1) * mm, "radius": 3.18 * mm});
            skCircle(sketch, "E2.40.21.0", {"center": v(431.8, -190.5) * mm, "radius": 3.18 * mm});
            skCircle(sketch, "E2.40.22.0", {"center": v(431.8, -215.9) * mm, "radius": 3.18 * mm});
            skCircle(sketch, "E2.40.23.0", {"center": v(431.8, -241.3) * mm, "radius": 3.18 * mm});
            skCircle(sketch, "E2.40.24.0", {"center": v(431.8, -266.7) * mm, "radius": 3.18 * mm});
            skCircle(sketch, "E2.40.25.0", {"center": v(431.8, -292.1) * mm, "radius": 3.18 * mm});
            skCircle(sketch, "E2.40.26.0", {"center": v(431.8, -317.5) * mm, "radius": 3.18 * mm});
            skCircle(sketch, "E2.40.27.0", {"center": v(431.8, -342.9) * mm, "radius": 3.18 * mm});
            skCircle(sketch, "E2.41.0.0", {"center": v(457.2, 342.9) * mm, "radius": 3.18 * mm});
            skCircle(sketch, "E2.41.1.0", {"center": v(457.2, 317.5) * mm, "radius": 3.18 * mm});
            skCircle(sketch, "E2.41.2.0", {"center": v(457.2, 292.1) * mm, "radius": 3.18 * mm});
            skCircle(sketch, "E2.41.3.0", {"center": v(457.2, 266.7) * mm, "radius": 3.18 * mm});
            skCircle(sketch, "E2.41.4.0", {"center": v(457.2, 241.3) * mm, "radius": 3.18 * mm});
            skCircle(sketch, "E2.41.5.0", {"center": v(457.2, 215.9) * mm, "radius": 3.18 * mm});
            skCircle(sketch, "E2.41.6.0", {"center": v(457.2, 190.5) * mm, "radius": 3.18 * mm});
            skCircle(sketch, "E2.41.7.0", {"center": v(457.2, 165.1) * mm, "radius": 3.18 * mm});
            skCircle(sketch, "E2.41.8.0", {"center": v(457.2, 139.7) * mm, "radius": 3.18 * mm});
            skCircle(sketch, "E2.41.9.0", {"center": v(457.2, 114.3) * mm, "radius": 3.18 * mm});
            skCircle(sketch, "E2.41.10.0", {"center": v(457.2, 88.9) * mm, "radius": 3.18 * mm});
            skCircle(sketch, "E2.41.11.0", {"center": v(457.2, 63.5) * mm, "radius": 3.18 * mm});
            skCircle(sketch, "E2.41.12.0", {"center": v(457.2, 38.1) * mm, "radius": 3.18 * mm});
            skCircle(sketch, "E2.41.13.0", {"center": v(457.2, 12.7) * mm, "radius": 3.18 * mm});
            skCircle(sketch, "E2.41.14.0", {"center": v(457.2, -12.7) * mm, "radius": 3.18 * mm});
            skCircle(sketch, "E2.41.15.0", {"center": v(457.2, -38.1) * mm, "radius": 3.18 * mm});
            skCircle(sketch, "E2.41.16.0", {"center": v(457.2, -63.5) * mm, "radius": 3.18 * mm});
            skCircle(sketch, "E2.41.17.0", {"center": v(457.2, -88.9) * mm, "radius": 3.18 * mm});
            skCircle(sketch, "E2.41.18.0", {"center": v(457.2, -114.3) * mm, "radius": 3.18 * mm});
            skCircle(sketch, "E2.41.19.0", {"center": v(457.2, -139.7) * mm, "radius": 3.18 * mm});
            skCircle(sketch, "E2.41.20.0", {"center": v(457.2, -165.1) * mm, "radius": 3.18 * mm});
            skCircle(sketch, "E2.41.21.0", {"center": v(457.2, -190.5) * mm, "radius": 3.18 * mm});
            skCircle(sketch, "E2.41.22.0", {"center": v(457.2, -215.9) * mm, "radius": 3.18 * mm});
            skCircle(sketch, "E2.41.23.0", {"center": v(457.2, -241.3) * mm, "radius": 3.18 * mm});
            skCircle(sketch, "E2.41.24.0", {"center": v(457.2, -266.7) * mm, "radius": 3.18 * mm});
            skCircle(sketch, "E2.41.25.0", {"center": v(457.2, -292.1) * mm, "radius": 3.18 * mm});
            skCircle(sketch, "E2.41.26.0", {"center": v(457.2, -317.5) * mm, "radius": 3.18 * mm});
            skCircle(sketch, "E2.41.27.0", {"center": v(457.2, -342.9) * mm, "radius": 3.18 * mm});
            skCircle(sketch, "E2.42.0.0", {"center": v(482.6, 342.9) * mm, "radius": 3.18 * mm});
            skCircle(sketch, "E2.42.1.0", {"center": v(482.6, 317.5) * mm, "radius": 3.18 * mm});
            skCircle(sketch, "E2.42.2.0", {"center": v(482.6, 292.1) * mm, "radius": 3.18 * mm});
            skCircle(sketch, "E2.42.3.0", {"center": v(482.6, 266.7) * mm, "radius": 3.18 * mm});
            skCircle(sketch, "E2.42.4.0", {"center": v(482.6, 241.3) * mm, "radius": 3.18 * mm});
            skCircle(sketch, "E2.42.5.0", {"center": v(482.6, 215.9) * mm, "radius": 3.18 * mm});
            skCircle(sketch, "E2.42.6.0", {"center": v(482.6, 190.5) * mm, "radius": 3.18 * mm});
            skCircle(sketch, "E2.42.7.0", {"center": v(482.6, 165.1) * mm, "radius": 3.18 * mm});
            skCircle(sketch, "E2.42.8.0", {"center": v(482.6, 139.7) * mm, "radius": 3.18 * mm});
            skCircle(sketch, "E2.42.9.0", {"center": v(482.6, 114.3) * mm, "radius": 3.18 * mm});
            skCircle(sketch, "E2.42.10.0", {"center": v(482.6, 88.9) * mm, "radius": 3.18 * mm});
            skCircle(sketch, "E2.42.11.0", {"center": v(482.6, 63.5) * mm, "radius": 3.18 * mm});
            skCircle(sketch, "E2.42.12.0", {"center": v(482.6, 38.1) * mm, "radius": 3.18 * mm});
            skCircle(sketch, "E2.42.13.0", {"center": v(482.6, 12.7) * mm, "radius": 3.18 * mm});
            skCircle(sketch, "E2.42.14.0", {"center": v(482.6, -12.7) * mm, "radius": 3.18 * mm});
            skCircle(sketch, "E2.42.15.0", {"center": v(482.6, -38.1) * mm, "radius": 3.18 * mm});
            skCircle(sketch, "E2.42.16.0", {"center": v(482.6, -63.5) * mm, "radius": 3.18 * mm});
            skCircle(sketch, "E2.42.17.0", {"center": v(482.6, -88.9) * mm, "radius": 3.18 * mm});
            skCircle(sketch, "E2.42.18.0", {"center": v(482.6, -114.3) * mm, "radius": 3.18 * mm});
            skCircle(sketch, "E2.42.19.0", {"center": v(482.6, -139.7) * mm, "radius": 3.18 * mm});
            skCircle(sketch, "E2.42.20.0", {"center": v(482.6, -165.1) * mm, "radius": 3.18 * mm});
            skCircle(sketch, "E2.42.21.0", {"center": v(482.6, -190.5) * mm, "radius": 3.18 * mm});
            skCircle(sketch, "E2.42.22.0", {"center": v(482.6, -215.9) * mm, "radius": 3.18 * mm});
            skCircle(sketch, "E2.42.23.0", {"center": v(482.6, -241.3) * mm, "radius": 3.18 * mm});
            skCircle(sketch, "E2.42.24.0", {"center": v(482.6, -266.7) * mm, "radius": 3.18 * mm});
            skCircle(sketch, "E2.42.25.0", {"center": v(482.6, -292.1) * mm, "radius": 3.18 * mm});
            skCircle(sketch, "E2.42.26.0", {"center": v(482.6, -317.5) * mm, "radius": 3.18 * mm});
            skCircle(sketch, "E2.42.27.0", {"center": v(482.6, -342.9) * mm, "radius": 3.18 * mm});
            skCircle(sketch, "E2.43.0.0", {"center": v(508, 342.9) * mm, "radius": 3.18 * mm});
            skCircle(sketch, "E2.43.1.0", {"center": v(508, 317.5) * mm, "radius": 3.18 * mm});
            skCircle(sketch, "E2.43.2.0", {"center": v(508, 292.1) * mm, "radius": 3.18 * mm});
            skCircle(sketch, "E2.43.3.0", {"center": v(508, 266.7) * mm, "radius": 3.18 * mm});
            skCircle(sketch, "E2.43.4.0", {"center": v(508, 241.3) * mm, "radius": 3.18 * mm});
            skCircle(sketch, "E2.43.5.0", {"center": v(508, 215.9) * mm, "radius": 3.18 * mm});
            skCircle(sketch, "E2.43.6.0", {"center": v(508, 190.5) * mm, "radius": 3.18 * mm});
            skCircle(sketch, "E2.43.7.0", {"center": v(508, 165.1) * mm, "radius": 3.18 * mm});
            skCircle(sketch, "E2.43.8.0", {"center": v(508, 139.7) * mm, "radius": 3.18 * mm});
            skCircle(sketch, "E2.43.9.0", {"center": v(508, 114.3) * mm, "radius": 3.18 * mm});
            skCircle(sketch, "E2.43.10.0", {"center": v(508, 88.9) * mm, "radius": 3.18 * mm});
            skCircle(sketch, "E2.43.11.0", {"center": v(508, 63.5) * mm, "radius": 3.18 * mm});
            skCircle(sketch, "E2.43.12.0", {"center": v(508, 38.1) * mm, "radius": 3.18 * mm});
            skCircle(sketch, "E2.43.13.0", {"center": v(508, 12.7) * mm, "radius": 3.18 * mm});
            skCircle(sketch, "E2.43.14.0", {"center": v(508, -12.7) * mm, "radius": 3.18 * mm});
            skCircle(sketch, "E2.43.15.0", {"center": v(508, -38.1) * mm, "radius": 3.18 * mm});
            skCircle(sketch, "E2.43.16.0", {"center": v(508, -63.5) * mm, "radius": 3.18 * mm});
            skCircle(sketch, "E2.43.17.0", {"center": v(508, -88.9) * mm, "radius": 3.18 * mm});
            skCircle(sketch, "E2.43.18.0", {"center": v(508, -114.3) * mm, "radius": 3.18 * mm});
            skCircle(sketch, "E2.43.19.0", {"center": v(508, -139.7) * mm, "radius": 3.18 * mm});
            skCircle(sketch, "E2.43.20.0", {"center": v(508, -165.1) * mm, "radius": 3.18 * mm});
            skCircle(sketch, "E2.43.21.0", {"center": v(508, -190.5) * mm, "radius": 3.18 * mm});
            skCircle(sketch, "E2.43.22.0", {"center": v(508, -215.9) * mm, "radius": 3.18 * mm});
            skCircle(sketch, "E2.43.23.0", {"center": v(508, -241.3) * mm, "radius": 3.18 * mm});
            skCircle(sketch, "E2.43.24.0", {"center": v(508, -266.7) * mm, "radius": 3.18 * mm});
            skCircle(sketch, "E2.43.25.0", {"center": v(508, -292.1) * mm, "radius": 3.18 * mm});
            skCircle(sketch, "E2.43.26.0", {"center": v(508, -317.5) * mm, "radius": 3.18 * mm});
            skCircle(sketch, "E2.43.27.0", {"center": v(508, -342.9) * mm, "radius": 3.18 * mm});
            skCircle(sketch, "E2.44.0.0", {"center": v(533.4, 342.9) * mm, "radius": 3.18 * mm});
            skCircle(sketch, "E2.44.1.0", {"center": v(533.4, 317.5) * mm, "radius": 3.18 * mm});
            skCircle(sketch, "E2.44.2.0", {"center": v(533.4, 292.1) * mm, "radius": 3.18 * mm});
            skCircle(sketch, "E2.44.3.0", {"center": v(533.4, 266.7) * mm, "radius": 3.18 * mm});
            skCircle(sketch, "E2.44.4.0", {"center": v(533.4, 241.3) * mm, "radius": 3.18 * mm});
            skCircle(sketch, "E2.44.5.0", {"center": v(533.4, 215.9) * mm, "radius": 3.18 * mm});
            skCircle(sketch, "E2.44.6.0", {"center": v(533.4, 190.5) * mm, "radius": 3.18 * mm});
            skCircle(sketch, "E2.44.7.0", {"center": v(533.4, 165.1) * mm, "radius": 3.18 * mm});
            skCircle(sketch, "E2.44.8.0", {"center": v(533.4, 139.7) * mm, "radius": 3.18 * mm});
            skCircle(sketch, "E2.44.9.0", {"center": v(533.4, 114.3) * mm, "radius": 3.18 * mm});
            skCircle(sketch, "E2.44.10.0", {"center": v(533.4, 88.9) * mm, "radius": 3.18 * mm});
            skCircle(sketch, "E2.44.11.0", {"center": v(533.4, 63.5) * mm, "radius": 3.18 * mm});
            skCircle(sketch, "E2.44.12.0", {"center": v(533.4, 38.1) * mm, "radius": 3.18 * mm});
            skCircle(sketch, "E2.44.13.0", {"center": v(533.4, 12.7) * mm, "radius": 3.18 * mm});
            skCircle(sketch, "E2.44.14.0", {"center": v(533.4, -12.7) * mm, "radius": 3.18 * mm});
            skCircle(sketch, "E2.44.15.0", {"center": v(533.4, -38.1) * mm, "radius": 3.18 * mm});
            skCircle(sketch, "E2.44.16.0", {"center": v(533.4, -63.5) * mm, "radius": 3.18 * mm});
            skCircle(sketch, "E2.44.17.0", {"center": v(533.4, -88.9) * mm, "radius": 3.18 * mm});
            skCircle(sketch, "E2.44.18.0", {"center": v(533.4, -114.3) * mm, "radius": 3.18 * mm});
            skCircle(sketch, "E2.44.19.0", {"center": v(533.4, -139.7) * mm, "radius": 3.18 * mm});
            skCircle(sketch, "E2.44.20.0", {"center": v(533.4, -165.1) * mm, "radius": 3.18 * mm});
            skCircle(sketch, "E2.44.21.0", {"center": v(533.4, -190.5) * mm, "radius": 3.18 * mm});
            skCircle(sketch, "E2.44.22.0", {"center": v(533.4, -215.9) * mm, "radius": 3.18 * mm});
            skCircle(sketch, "E2.44.23.0", {"center": v(533.4, -241.3) * mm, "radius": 3.18 * mm});
            skCircle(sketch, "E2.44.24.0", {"center": v(533.4, -266.7) * mm, "radius": 3.18 * mm});
            skCircle(sketch, "E2.44.25.0", {"center": v(533.4, -292.1) * mm, "radius": 3.18 * mm});
            skCircle(sketch, "E2.44.26.0", {"center": v(533.4, -317.5) * mm, "radius": 3.18 * mm});
            skCircle(sketch, "E2.44.27.0", {"center": v(533.4, -342.9) * mm, "radius": 3.18 * mm});
            skCircle(sketch, "E2.45.0.0", {"center": v(558.8, 342.9) * mm, "radius": 3.18 * mm});
            skCircle(sketch, "E2.45.1.0", {"center": v(558.8, 317.5) * mm, "radius": 3.18 * mm});
            skCircle(sketch, "E2.45.2.0", {"center": v(558.8, 292.1) * mm, "radius": 3.18 * mm});
            skCircle(sketch, "E2.45.3.0", {"center": v(558.8, 266.7) * mm, "radius": 3.18 * mm});
            skCircle(sketch, "E2.45.4.0", {"center": v(558.8, 241.3) * mm, "radius": 3.18 * mm});
            skCircle(sketch, "E2.45.5.0", {"center": v(558.8, 215.9) * mm, "radius": 3.18 * mm});
            skCircle(sketch, "E2.45.6.0", {"center": v(558.8, 190.5) * mm, "radius": 3.18 * mm});
            skCircle(sketch, "E2.45.7.0", {"center": v(558.8, 165.1) * mm, "radius": 3.18 * mm});
            skCircle(sketch, "E2.45.8.0", {"center": v(558.8, 139.7) * mm, "radius": 3.18 * mm});
            skCircle(sketch, "E2.45.9.0", {"center": v(558.8, 114.3) * mm, "radius": 3.18 * mm});
            skCircle(sketch, "E2.45.10.0", {"center": v(558.8, 88.9) * mm, "radius": 3.18 * mm});
            skCircle(sketch, "E2.45.11.0", {"center": v(558.8, 63.5) * mm, "radius": 3.18 * mm});
            skCircle(sketch, "E2.45.12.0", {"center": v(558.8, 38.1) * mm, "radius": 3.18 * mm});
            skCircle(sketch, "E2.45.13.0", {"center": v(558.8, 12.7) * mm, "radius": 3.18 * mm});
            skCircle(sketch, "E2.45.14.0", {"center": v(558.8, -12.7) * mm, "radius": 3.18 * mm});
            skCircle(sketch, "E2.45.15.0", {"center": v(558.8, -38.1) * mm, "radius": 3.18 * mm});
            skCircle(sketch, "E2.45.16.0", {"center": v(558.8, -63.5) * mm, "radius": 3.18 * mm});
            skCircle(sketch, "E2.45.17.0", {"center": v(558.8, -88.9) * mm, "radius": 3.18 * mm});
            skCircle(sketch, "E2.45.18.0", {"center": v(558.8, -114.3) * mm, "radius": 3.18 * mm});
            skCircle(sketch, "E2.45.19.0", {"center": v(558.8, -139.7) * mm, "radius": 3.18 * mm});
            skCircle(sketch, "E2.45.20.0", {"center": v(558.8, -165.1) * mm, "radius": 3.18 * mm});
            skCircle(sketch, "E2.45.21.0", {"center": v(558.8, -190.5) * mm, "radius": 3.18 * mm});
            skCircle(sketch, "E2.45.22.0", {"center": v(558.8, -215.9) * mm, "radius": 3.18 * mm});
            skCircle(sketch, "E2.45.23.0", {"center": v(558.8, -241.3) * mm, "radius": 3.18 * mm});
            skCircle(sketch, "E2.45.24.0", {"center": v(558.8, -266.7) * mm, "radius": 3.18 * mm});
            skCircle(sketch, "E2.45.25.0", {"center": v(558.8, -292.1) * mm, "radius": 3.18 * mm});
            skCircle(sketch, "E2.45.26.0", {"center": v(558.8, -317.5) * mm, "radius": 3.18 * mm});
            skCircle(sketch, "E2.45.27.0", {"center": v(558.8, -342.9) * mm, "radius": 3.18 * mm});
            skCircle(sketch, "E2.46.0.0", {"center": v(584.2, 342.9) * mm, "radius": 3.18 * mm});
            skCircle(sketch, "E2.46.1.0", {"center": v(584.2, 317.5) * mm, "radius": 3.18 * mm});
            skCircle(sketch, "E2.46.2.0", {"center": v(584.2, 292.1) * mm, "radius": 3.18 * mm});
            skCircle(sketch, "E2.46.3.0", {"center": v(584.2, 266.7) * mm, "radius": 3.18 * mm});
            skCircle(sketch, "E2.46.4.0", {"center": v(584.2, 241.3) * mm, "radius": 3.18 * mm});
            skCircle(sketch, "E2.46.5.0", {"center": v(584.2, 215.9) * mm, "radius": 3.18 * mm});
            skCircle(sketch, "E2.46.6.0", {"center": v(584.2, 190.5) * mm, "radius": 3.18 * mm});
            skCircle(sketch, "E2.46.7.0", {"center": v(584.2, 165.1) * mm, "radius": 3.18 * mm});
            skCircle(sketch, "E2.46.8.0", {"center": v(584.2, 139.7) * mm, "radius": 3.18 * mm});
            skCircle(sketch, "E2.46.9.0", {"center": v(584.2, 114.3) * mm, "radius": 3.18 * mm});
            skCircle(sketch, "E2.46.10.0", {"center": v(584.2, 88.9) * mm, "radius": 3.18 * mm});
            skCircle(sketch, "E2.46.11.0", {"center": v(584.2, 63.5) * mm, "radius": 3.18 * mm});
            skCircle(sketch, "E2.46.12.0", {"center": v(584.2, 38.1) * mm, "radius": 3.18 * mm});
            skCircle(sketch, "E2.46.13.0", {"center": v(584.2, 12.7) * mm, "radius": 3.18 * mm});
            skCircle(sketch, "E2.46.14.0", {"center": v(584.2, -12.7) * mm, "radius": 3.18 * mm});
            skCircle(sketch, "E2.46.15.0", {"center": v(584.2, -38.1) * mm, "radius": 3.18 * mm});
            skCircle(sketch, "E2.46.16.0", {"center": v(584.2, -63.5) * mm, "radius": 3.18 * mm});
            skCircle(sketch, "E2.46.17.0", {"center": v(584.2, -88.9) * mm, "radius": 3.18 * mm});
            skCircle(sketch, "E2.46.18.0", {"center": v(584.2, -114.3) * mm, "radius": 3.18 * mm});
            skCircle(sketch, "E2.46.19.0", {"center": v(584.2, -139.7) * mm, "radius": 3.18 * mm});
            skCircle(sketch, "E2.46.20.0", {"center": v(584.2, -165.1) * mm, "radius": 3.18 * mm});
            skCircle(sketch, "E2.46.21.0", {"center": v(584.2, -190.5) * mm, "radius": 3.18 * mm});
            skCircle(sketch, "E2.46.22.0", {"center": v(584.2, -215.9) * mm, "radius": 3.18 * mm});
            skCircle(sketch, "E2.46.23.0", {"center": v(584.2, -241.3) * mm, "radius": 3.18 * mm});
            skCircle(sketch, "E2.46.24.0", {"center": v(584.2, -266.7) * mm, "radius": 3.18 * mm});
            skCircle(sketch, "E2.46.25.0", {"center": v(584.2, -292.1) * mm, "radius": 3.18 * mm});
            skCircle(sketch, "E2.46.26.0", {"center": v(584.2, -317.5) * mm, "radius": 3.18 * mm});
            skCircle(sketch, "E2.46.27.0", {"center": v(584.2, -342.9) * mm, "radius": 3.18 * mm});
            skLineSegment(sketch, "E2.direction1", {"start": v(-584.2, 342.9) * mm, "end": v(-558.8, 342.9) * mm, "construction": true});
            skLineSegment(sketch, "E2.direction2", {"start": v(-584.2, 342.9) * mm, "end": v(-584.2, 317.5) * mm, "construction": true});
            skSolve(sketch);
        }
        {
            var Q0;
            Q0=makeQuery(id+"F0.imprint","IMPRINT",FACE,{"disambiguationData":[TD([[makeQuery(id+"F0.imprint","IMPRINT",EDGE,{"derivedFrom":sQuery(id+"F0.wireOp",EDGE,"E0.bottom")}),1.0]])]});
            extrude(context, id + "F1", {"entities" : qUnion([Q0]), "depth" : 3.17 * mm, "offsetDistance" : 25.4 * mm});
        }
    });
